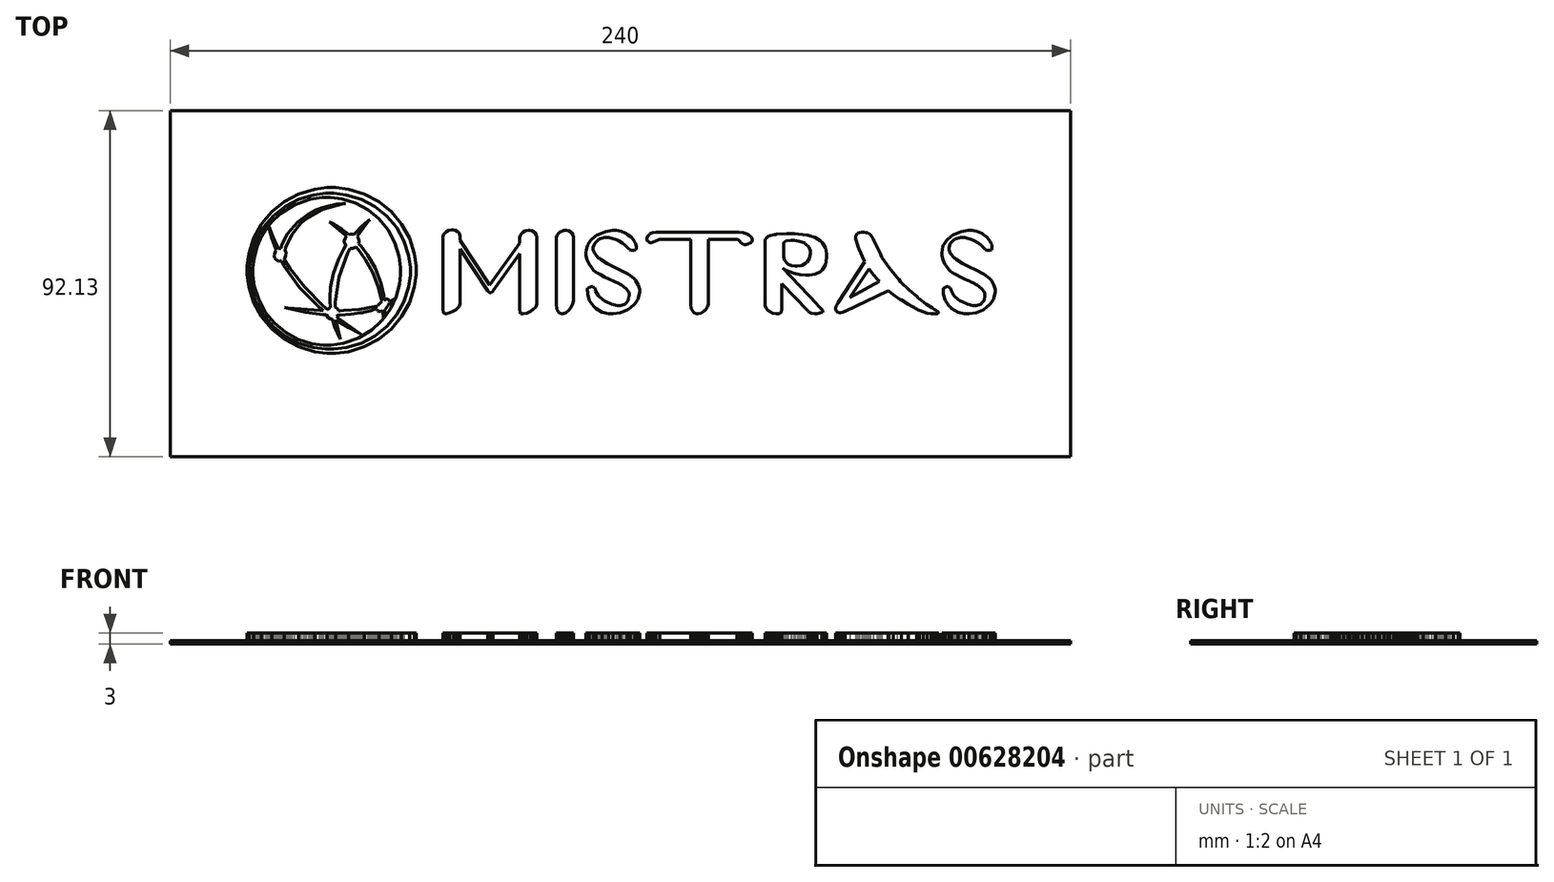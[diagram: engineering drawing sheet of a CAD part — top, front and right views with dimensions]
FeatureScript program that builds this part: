
annotation { "Feature Type Name" : "Feature", "Feature Type Description" : "" }
export const myFeature = defineFeature(function(context is Context, id is Id, definition is map)
    precondition{}
    {
        {
            var Q0;
            Q0=qCreatedBy(makeId("Top.planeOp"),FACE);
            var sketch = newSketch(context, id + "F0", { "sketchPlane" : qUnion([Q0])});
            skLineSegment(sketch, "E0.bottom", {"start": v(-94.91, 44.04) * mm, "end": v(105.09, 44.04) * mm, "construction": true});
            skLineSegment(sketch, "E0.top", {"start": v(-94.91, -8.1) * mm, "end": v(105.09, -8.1) * mm, "construction": true});
            skLineSegment(sketch, "E0.left", {"start": v(-94.91, 44.04) * mm, "end": v(-94.91, -8.1) * mm, "construction": true});
            skLineSegment(sketch, "E0.right", {"start": v(105.09, 44.04) * mm, "end": v(105.09, -8.1) * mm, "construction": true});
            skLineSegment(sketch, "E1", {"start": v(-21.8, 26) * mm, "end": v(-28.84, 16.06) * mm});
            skLineSegment(sketch, "E2", {"start": v(-28.84, 16.06) * mm, "end": v(-28.9, 15.99) * mm});
            skLineSegment(sketch, "E3", {"start": v(-28.9, 15.99) * mm, "end": v(-29.42, 15.62) * mm});
            skLineSegment(sketch, "E4", {"start": v(-29.42, 15.62) * mm, "end": v(-29.6, 15.62) * mm});
            skLineSegment(sketch, "E5", {"start": v(-29.6, 15.62) * mm, "end": v(-29.76, 15.62) * mm});
            skLineSegment(sketch, "E6", {"start": v(-29.76, 15.62) * mm, "end": v(-30.22, 15.97) * mm});
            skLineSegment(sketch, "E7", {"start": v(-30.22, 15.97) * mm, "end": v(-30.26, 16.05) * mm});
            skLineSegment(sketch, "E8", {"start": v(-30.26, 16.05) * mm, "end": v(-37.6, 27.26) * mm});
            skLineSegment(sketch, "E9", {"start": v(-37.6, 27.26) * mm, "end": v(-37.6, 12.97) * mm});
            skLineSegment(sketch, "E10", {"start": v(-37.6, 12.97) * mm, "end": v(-37.6, 12.7) * mm});
            skLineSegment(sketch, "E11", {"start": v(-37.6, 12.7) * mm, "end": v(-37.96, 11.88) * mm});
            skLineSegment(sketch, "E12", {"start": v(-37.96, 11.88) * mm, "end": v(-38.8, 11.04) * mm});
            skLineSegment(sketch, "E13", {"start": v(-38.8, 11.04) * mm, "end": v(-39.05, 10.88) * mm});
            skLineSegment(sketch, "E14", {"start": v(-39.05, 10.88) * mm, "end": v(-39.3, 10.73) * mm});
            skLineSegment(sketch, "E15", {"start": v(-39.3, 10.73) * mm, "end": v(-40.42, 10.17) * mm});
            skLineSegment(sketch, "E16", {"start": v(-40.42, 10.17) * mm, "end": v(-41.31, 9.94) * mm});
            skLineSegment(sketch, "E17", {"start": v(-41.31, 9.94) * mm, "end": v(-41.61, 9.94) * mm});
            skLineSegment(sketch, "E18", {"start": v(-41.61, 9.94) * mm, "end": v(-41.74, 9.94) * mm});
            skLineSegment(sketch, "E19", {"start": v(-41.74, 9.94) * mm, "end": v(-42.13, 10.22) * mm});
            skLineSegment(sketch, "E20", {"start": v(-42.13, 10.22) * mm, "end": v(-42.14, 10.27) * mm});
            skLineSegment(sketch, "E21", {"start": v(-42.14, 10.27) * mm, "end": v(-42.15, 10.33) * mm});
            skLineSegment(sketch, "E22", {"start": v(-42.15, 10.33) * mm, "end": v(-42.2, 11.12) * mm});
            skLineSegment(sketch, "E23", {"start": v(-42.2, 11.12) * mm, "end": v(-42.2, 11.22) * mm});
            skLineSegment(sketch, "E24", {"start": v(-42.2, 11.22) * mm, "end": v(-42.21, 11.32) * mm});
            skLineSegment(sketch, "E25", {"start": v(-42.21, 11.32) * mm, "end": v(-42.23, 12.56) * mm});
            skLineSegment(sketch, "E26", {"start": v(-42.23, 12.56) * mm, "end": v(-42.23, 12.97) * mm});
            skLineSegment(sketch, "E27", {"start": v(-42.23, 12.97) * mm, "end": v(-42.23, 30.16) * mm});
            skLineSegment(sketch, "E28", {"start": v(-42.23, 30.16) * mm, "end": v(-42.23, 30.38) * mm});
            skLineSegment(sketch, "E29", {"start": v(-42.23, 30.38) * mm, "end": v(-42.05, 31.03) * mm});
            skLineSegment(sketch, "E30", {"start": v(-42.05, 31.03) * mm, "end": v(-41.6, 31.63) * mm});
            skLineSegment(sketch, "E31", {"start": v(-41.6, 31.63) * mm, "end": v(-41.48, 31.73) * mm});
            skLineSegment(sketch, "E32", {"start": v(-41.48, 31.73) * mm, "end": v(-41.35, 31.83) * mm});
            skLineSegment(sketch, "E33", {"start": v(-41.35, 31.83) * mm, "end": v(-40.67, 32.2) * mm});
            skLineSegment(sketch, "E34", {"start": v(-40.67, 32.2) * mm, "end": v(-39.98, 32.35) * mm});
            skLineSegment(sketch, "E35", {"start": v(-39.98, 32.35) * mm, "end": v(-39.75, 32.35) * mm});
            skLineSegment(sketch, "E36", {"start": v(-39.75, 32.35) * mm, "end": v(-39.53, 32.35) * mm});
            skLineSegment(sketch, "E37", {"start": v(-39.53, 32.35) * mm, "end": v(-38.87, 32.21) * mm});
            skLineSegment(sketch, "E38", {"start": v(-38.87, 32.21) * mm, "end": v(-38.28, 31.88) * mm});
            skLineSegment(sketch, "E39", {"start": v(-38.28, 31.88) * mm, "end": v(-38.18, 31.78) * mm});
            skLineSegment(sketch, "E40", {"start": v(-38.18, 31.78) * mm, "end": v(-38.09, 31.7) * mm});
            skLineSegment(sketch, "E41", {"start": v(-38.09, 31.7) * mm, "end": v(-37.74, 31.15) * mm});
            skLineSegment(sketch, "E42", {"start": v(-37.74, 31.15) * mm, "end": v(-37.6, 30.57) * mm});
            skLineSegment(sketch, "E43", {"start": v(-37.6, 30.57) * mm, "end": v(-37.6, 30.38) * mm});
            skLineSegment(sketch, "E44", {"start": v(-37.6, 30.38) * mm, "end": v(-37.6, 29.51) * mm});
            skLineSegment(sketch, "E45", {"start": v(-37.6, 29.51) * mm, "end": v(-29.82, 17.54) * mm});
            skLineSegment(sketch, "E46", {"start": v(-29.82, 17.54) * mm, "end": v(-21.8, 28.81) * mm});
            skLineSegment(sketch, "E47", {"start": v(-21.8, 28.81) * mm, "end": v(-21.8, 30) * mm});
            skLineSegment(sketch, "E48", {"start": v(-21.8, 30) * mm, "end": v(-21.8, 30.22) * mm});
            skLineSegment(sketch, "E49", {"start": v(-21.8, 30.22) * mm, "end": v(-21.6, 30.87) * mm});
            skLineSegment(sketch, "E50", {"start": v(-21.6, 30.87) * mm, "end": v(-21.17, 31.47) * mm});
            skLineSegment(sketch, "E51", {"start": v(-21.17, 31.47) * mm, "end": v(-21.04, 31.57) * mm});
            skLineSegment(sketch, "E52", {"start": v(-21.04, 31.57) * mm, "end": v(-20.92, 31.67) * mm});
            skLineSegment(sketch, "E53", {"start": v(-20.92, 31.67) * mm, "end": v(-20.23, 32.03) * mm});
            skLineSegment(sketch, "E54", {"start": v(-20.23, 32.03) * mm, "end": v(-19.54, 32.19) * mm});
            skLineSegment(sketch, "E55", {"start": v(-19.54, 32.19) * mm, "end": v(-19.31, 32.19) * mm});
            skLineSegment(sketch, "E56", {"start": v(-19.31, 32.19) * mm, "end": v(-19.1, 32.19) * mm});
            skLineSegment(sketch, "E57", {"start": v(-19.1, 32.19) * mm, "end": v(-18.44, 32.05) * mm});
            skLineSegment(sketch, "E58", {"start": v(-18.44, 32.05) * mm, "end": v(-17.85, 31.72) * mm});
            skLineSegment(sketch, "E59", {"start": v(-17.85, 31.72) * mm, "end": v(-17.75, 31.62) * mm});
            skLineSegment(sketch, "E60", {"start": v(-17.75, 31.62) * mm, "end": v(-17.65, 31.53) * mm});
            skLineSegment(sketch, "E61", {"start": v(-17.65, 31.53) * mm, "end": v(-17.3, 30.99) * mm});
            skLineSegment(sketch, "E62", {"start": v(-17.3, 30.99) * mm, "end": v(-17.15, 30.41) * mm});
            skLineSegment(sketch, "E63", {"start": v(-17.15, 30.41) * mm, "end": v(-17.15, 30.22) * mm});
            skLineSegment(sketch, "E64", {"start": v(-17.15, 30.22) * mm, "end": v(-17.15, 12.8) * mm});
            skLineSegment(sketch, "E65", {"start": v(-17.15, 12.8) * mm, "end": v(-17.15, 12.54) * mm});
            skLineSegment(sketch, "E66", {"start": v(-17.15, 12.54) * mm, "end": v(-17.51, 11.75) * mm});
            skLineSegment(sketch, "E67", {"start": v(-17.51, 11.75) * mm, "end": v(-18.35, 10.96) * mm});
            skLineSegment(sketch, "E68", {"start": v(-18.35, 10.96) * mm, "end": v(-18.59, 10.81) * mm});
            skLineSegment(sketch, "E69", {"start": v(-18.59, 10.81) * mm, "end": v(-18.83, 10.67) * mm});
            skLineSegment(sketch, "E70", {"start": v(-18.83, 10.67) * mm, "end": v(-19.94, 10.16) * mm});
            skLineSegment(sketch, "E71", {"start": v(-19.94, 10.16) * mm, "end": v(-20.83, 9.94) * mm});
            skLineSegment(sketch, "E72", {"start": v(-20.83, 9.94) * mm, "end": v(-21.12, 9.94) * mm});
            skLineSegment(sketch, "E73", {"start": v(-21.12, 9.94) * mm, "end": v(-21.23, 9.94) * mm});
            skLineSegment(sketch, "E74", {"start": v(-21.23, 9.94) * mm, "end": v(-21.54, 10.02) * mm});
            skLineSegment(sketch, "E75", {"start": v(-21.54, 10.02) * mm, "end": v(-21.7, 10.23) * mm});
            skLineSegment(sketch, "E76", {"start": v(-21.7, 10.23) * mm, "end": v(-21.7, 10.29) * mm});
            skLineSegment(sketch, "E77", {"start": v(-21.7, 10.29) * mm, "end": v(-21.71, 10.35) * mm});
            skLineSegment(sketch, "E78", {"start": v(-21.71, 10.35) * mm, "end": v(-21.77, 11.08) * mm});
            skLineSegment(sketch, "E79", {"start": v(-21.77, 11.08) * mm, "end": v(-21.77, 11.17) * mm});
            skLineSegment(sketch, "E80", {"start": v(-21.77, 11.17) * mm, "end": v(-21.77, 11.26) * mm});
            skLineSegment(sketch, "E81", {"start": v(-21.77, 11.26) * mm, "end": v(-21.8, 12.42) * mm});
            skLineSegment(sketch, "E82", {"start": v(-21.8, 12.42) * mm, "end": v(-21.8, 12.8) * mm});
            skLineSegment(sketch, "E83", {"start": v(-21.8, 12.8) * mm, "end": v(-21.8, 26) * mm});
            skLineSegment(sketch, "E84", {"start": v(-7.37, 30.21) * mm, "end": v(-7.37, 13.75) * mm});
            skLineSegment(sketch, "E85", {"start": v(-7.37, 13.75) * mm, "end": v(-7.37, 13.45) * mm});
            skLineSegment(sketch, "E86", {"start": v(-7.37, 13.45) * mm, "end": v(-7.63, 12.54) * mm});
            skLineSegment(sketch, "E87", {"start": v(-7.63, 12.54) * mm, "end": v(-8.22, 11.48) * mm});
            skLineSegment(sketch, "E88", {"start": v(-8.22, 11.48) * mm, "end": v(-8.39, 11.26) * mm});
            skLineSegment(sketch, "E89", {"start": v(-8.39, 11.26) * mm, "end": v(-8.56, 11.04) * mm});
            skLineSegment(sketch, "E90", {"start": v(-8.56, 11.04) * mm, "end": v(-9.4, 10.27) * mm});
            skLineSegment(sketch, "E91", {"start": v(-9.4, 10.27) * mm, "end": v(-10.17, 9.94) * mm});
            skLineSegment(sketch, "E92", {"start": v(-10.17, 9.94) * mm, "end": v(-10.42, 9.94) * mm});
            skLineSegment(sketch, "E93", {"start": v(-10.42, 9.94) * mm, "end": v(-10.65, 9.94) * mm});
            skLineSegment(sketch, "E94", {"start": v(-10.65, 9.94) * mm, "end": v(-11.23, 10.26) * mm});
            skLineSegment(sketch, "E95", {"start": v(-11.23, 10.26) * mm, "end": v(-11.3, 10.33) * mm});
            skLineSegment(sketch, "E96", {"start": v(-11.3, 10.33) * mm, "end": v(-11.38, 10.4) * mm});
            skLineSegment(sketch, "E97", {"start": v(-11.38, 10.4) * mm, "end": v(-11.86, 11.19) * mm});
            skLineSegment(sketch, "E98", {"start": v(-11.86, 11.19) * mm, "end": v(-11.88, 11.28) * mm});
            skLineSegment(sketch, "E99", {"start": v(-11.88, 11.28) * mm, "end": v(-11.9, 11.37) * mm});
            skLineSegment(sketch, "E100", {"start": v(-11.9, 11.37) * mm, "end": v(-12.02, 12.44) * mm});
            skLineSegment(sketch, "E101", {"start": v(-12.02, 12.44) * mm, "end": v(-12.02, 12.8) * mm});
            skLineSegment(sketch, "E102", {"start": v(-12.02, 12.8) * mm, "end": v(-12.02, 30) * mm});
            skLineSegment(sketch, "E103", {"start": v(-12.02, 30) * mm, "end": v(-12.02, 30.21) * mm});
            skLineSegment(sketch, "E104", {"start": v(-12.02, 30.21) * mm, "end": v(-11.83, 30.86) * mm});
            skLineSegment(sketch, "E105", {"start": v(-11.83, 30.86) * mm, "end": v(-11.4, 31.46) * mm});
            skLineSegment(sketch, "E106", {"start": v(-11.4, 31.46) * mm, "end": v(-11.26, 31.56) * mm});
            skLineSegment(sketch, "E107", {"start": v(-11.26, 31.56) * mm, "end": v(-11.14, 31.67) * mm});
            skLineSegment(sketch, "E108", {"start": v(-11.14, 31.67) * mm, "end": v(-9.94, 32.18) * mm});
            skLineSegment(sketch, "E109", {"start": v(-9.94, 32.18) * mm, "end": v(-9.53, 32.18) * mm});
            skLineSegment(sketch, "E110", {"start": v(-9.53, 32.18) * mm, "end": v(-9.32, 32.18) * mm});
            skLineSegment(sketch, "E111", {"start": v(-9.32, 32.18) * mm, "end": v(-8.66, 32.04) * mm});
            skLineSegment(sketch, "E112", {"start": v(-8.66, 32.04) * mm, "end": v(-8.07, 31.71) * mm});
            skLineSegment(sketch, "E113", {"start": v(-8.07, 31.71) * mm, "end": v(-7.97, 31.62) * mm});
            skLineSegment(sketch, "E114", {"start": v(-7.97, 31.62) * mm, "end": v(-7.87, 31.52) * mm});
            skLineSegment(sketch, "E115", {"start": v(-7.87, 31.52) * mm, "end": v(-7.52, 30.98) * mm});
            skLineSegment(sketch, "E116", {"start": v(-7.52, 30.98) * mm, "end": v(-7.37, 30.4) * mm});
            skLineSegment(sketch, "E117", {"start": v(-7.37, 30.4) * mm, "end": v(-7.37, 30.21) * mm});
            skLineSegment(sketch, "E118", {"start": v(-1.61, 16.35) * mm, "end": v(-1.55, 16.07) * mm});
            skLineSegment(sketch, "E119", {"start": v(-1.55, 16.07) * mm, "end": v(-0.81, 14.79) * mm});
            skLineSegment(sketch, "E120", {"start": v(-0.81, 14.79) * mm, "end": v(0.46, 13.65) * mm});
            skLineSegment(sketch, "E121", {"start": v(0.46, 13.65) * mm, "end": v(0.8, 13.44) * mm});
            skLineSegment(sketch, "E122", {"start": v(0.8, 13.44) * mm, "end": v(1.12, 13.23) * mm});
            skLineSegment(sketch, "E123", {"start": v(1.12, 13.23) * mm, "end": v(2.78, 12.5) * mm});
            skLineSegment(sketch, "E124", {"start": v(2.78, 12.5) * mm, "end": v(4.25, 12.2) * mm});
            skLineSegment(sketch, "E125", {"start": v(4.25, 12.2) * mm, "end": v(4.74, 12.2) * mm});
            skLineSegment(sketch, "E126", {"start": v(4.74, 12.2) * mm, "end": v(5.16, 12.2) * mm});
            skLineSegment(sketch, "E127", {"start": v(5.16, 12.2) * mm, "end": v(6.33, 12.57) * mm});
            skLineSegment(sketch, "E128", {"start": v(6.33, 12.57) * mm, "end": v(6.44, 12.65) * mm});
            skLineSegment(sketch, "E129", {"start": v(6.44, 12.65) * mm, "end": v(6.55, 12.72) * mm});
            skLineSegment(sketch, "E130", {"start": v(6.55, 12.72) * mm, "end": v(7.2, 13.6) * mm});
            skLineSegment(sketch, "E131", {"start": v(7.2, 13.6) * mm, "end": v(7.22, 13.7) * mm});
            skLineSegment(sketch, "E132", {"start": v(7.22, 13.7) * mm, "end": v(7.24, 13.8) * mm});
            skLineSegment(sketch, "E133", {"start": v(7.24, 13.8) * mm, "end": v(7.37, 14.53) * mm});
            skLineSegment(sketch, "E134", {"start": v(7.37, 14.53) * mm, "end": v(7.37, 14.57) * mm});
            skLineSegment(sketch, "E135", {"start": v(7.37, 14.57) * mm, "end": v(7.38, 14.62) * mm});
            skLineSegment(sketch, "E136", {"start": v(7.38, 14.62) * mm, "end": v(7.41, 15.06) * mm});
            skLineSegment(sketch, "E137", {"start": v(7.41, 15.06) * mm, "end": v(7.41, 15.2) * mm});
            skLineSegment(sketch, "E138", {"start": v(7.41, 15.2) * mm, "end": v(7.41, 15.4) * mm});
            skLineSegment(sketch, "E139", {"start": v(7.41, 15.4) * mm, "end": v(7.19, 15.98) * mm});
            skLineSegment(sketch, "E140", {"start": v(7.19, 15.98) * mm, "end": v(6.52, 16.77) * mm});
            skLineSegment(sketch, "E141", {"start": v(6.52, 16.77) * mm, "end": v(5.4, 17.58) * mm});
            skLineSegment(sketch, "E142", {"start": v(5.4, 17.58) * mm, "end": v(4.23, 18.22) * mm});
            skLineSegment(sketch, "E143", {"start": v(4.23, 18.22) * mm, "end": v(3.83, 18.4) * mm});
            skLineSegment(sketch, "E144", {"start": v(3.83, 18.4) * mm, "end": v(3.42, 18.6) * mm});
            skLineSegment(sketch, "E145", {"start": v(3.42, 18.6) * mm, "end": v(2.2, 19.17) * mm});
            skLineSegment(sketch, "E146", {"start": v(2.2, 19.17) * mm, "end": v(0.86, 19.82) * mm});
            skLineSegment(sketch, "E147", {"start": v(0.86, 19.82) * mm, "end": v(-0.18, 20.33) * mm});
            skLineSegment(sketch, "E148", {"start": v(-0.18, 20.33) * mm, "end": v(-0.73, 20.62) * mm});
            skLineSegment(sketch, "E149", {"start": v(-0.73, 20.62) * mm, "end": v(-0.9, 20.72) * mm});
            skLineSegment(sketch, "E150", {"start": v(-0.9, 20.72) * mm, "end": v(-1.1, 20.84) * mm});
            skLineSegment(sketch, "E151", {"start": v(-1.1, 20.84) * mm, "end": v(-2.03, 21.6) * mm});
            skLineSegment(sketch, "E152", {"start": v(-2.03, 21.6) * mm, "end": v(-2.9, 22.64) * mm});
            skLineSegment(sketch, "E153", {"start": v(-2.9, 22.64) * mm, "end": v(-3.07, 22.9) * mm});
            skLineSegment(sketch, "E154", {"start": v(-3.07, 22.9) * mm, "end": v(-3.24, 23.14) * mm});
            skLineSegment(sketch, "E155", {"start": v(-3.24, 23.14) * mm, "end": v(-3.83, 24.44) * mm});
            skLineSegment(sketch, "E156", {"start": v(-3.83, 24.44) * mm, "end": v(-4.07, 25.66) * mm});
            skLineSegment(sketch, "E157", {"start": v(-4.07, 25.66) * mm, "end": v(-4.07, 26.06) * mm});
            skLineSegment(sketch, "E158", {"start": v(-4.07, 26.06) * mm, "end": v(-4.07, 26.3) * mm});
            skLineSegment(sketch, "E159", {"start": v(-4.07, 26.3) * mm, "end": v(-3.97, 26.98) * mm});
            skLineSegment(sketch, "E160", {"start": v(-3.97, 26.98) * mm, "end": v(-3.73, 28) * mm});
            skLineSegment(sketch, "E161", {"start": v(-3.73, 28) * mm, "end": v(-3.66, 28.22) * mm});
            skLineSegment(sketch, "E162", {"start": v(-3.66, 28.22) * mm, "end": v(-3.59, 28.46) * mm});
            skLineSegment(sketch, "E163", {"start": v(-3.59, 28.46) * mm, "end": v(-2.83, 29.6) * mm});
            skLineSegment(sketch, "E164", {"start": v(-2.83, 29.6) * mm, "end": v(-1.52, 30.7) * mm});
            skLineSegment(sketch, "E165", {"start": v(-1.52, 30.7) * mm, "end": v(-1.18, 30.9) * mm});
            skLineSegment(sketch, "E166", {"start": v(-1.18, 30.9) * mm, "end": v(-0.84, 31.12) * mm});
            skLineSegment(sketch, "E167", {"start": v(-0.84, 31.12) * mm, "end": v(1.04, 31.86) * mm});
            skLineSegment(sketch, "E168", {"start": v(1.04, 31.86) * mm, "end": v(2.96, 32.18) * mm});
            skLineSegment(sketch, "E169", {"start": v(2.96, 32.18) * mm, "end": v(3.6, 32.18) * mm});
            skLineSegment(sketch, "E170", {"start": v(3.6, 32.18) * mm, "end": v(4, 32.18) * mm});
            skLineSegment(sketch, "E171", {"start": v(4, 32.18) * mm, "end": v(5.22, 31.96) * mm});
            skLineSegment(sketch, "E172", {"start": v(5.22, 31.96) * mm, "end": v(6.47, 31.42) * mm});
            skLineSegment(sketch, "E173", {"start": v(6.47, 31.42) * mm, "end": v(6.71, 31.27) * mm});
            skLineSegment(sketch, "E174", {"start": v(6.71, 31.27) * mm, "end": v(6.95, 31.12) * mm});
            skLineSegment(sketch, "E175", {"start": v(6.95, 31.12) * mm, "end": v(7.91, 30.37) * mm});
            skLineSegment(sketch, "E176", {"start": v(7.91, 30.37) * mm, "end": v(8.57, 29.64) * mm});
            skLineSegment(sketch, "E177", {"start": v(8.57, 29.64) * mm, "end": v(8.66, 29.5) * mm});
            skLineSegment(sketch, "E178", {"start": v(8.66, 29.5) * mm, "end": v(8.74, 29.35) * mm});
            skLineSegment(sketch, "E179", {"start": v(8.74, 29.35) * mm, "end": v(9.06, 28.76) * mm});
            skLineSegment(sketch, "E180", {"start": v(9.06, 28.76) * mm, "end": v(9.24, 28.35) * mm});
            skLineSegment(sketch, "E181", {"start": v(9.24, 28.35) * mm, "end": v(9.25, 28.3) * mm});
            skLineSegment(sketch, "E182", {"start": v(9.25, 28.3) * mm, "end": v(9.27, 28.24) * mm});
            skLineSegment(sketch, "E183", {"start": v(9.27, 28.24) * mm, "end": v(9.33, 27.85) * mm});
            skLineSegment(sketch, "E184", {"start": v(9.33, 27.85) * mm, "end": v(9.33, 27.73) * mm});
            skLineSegment(sketch, "E185", {"start": v(9.33, 27.73) * mm, "end": v(9.33, 27.62) * mm});
            skLineSegment(sketch, "E186", {"start": v(9.33, 27.62) * mm, "end": v(9.29, 27.33) * mm});
            skLineSegment(sketch, "E187", {"start": v(9.29, 27.33) * mm, "end": v(9.28, 27.3) * mm});
            skLineSegment(sketch, "E188", {"start": v(9.28, 27.3) * mm, "end": v(9.27, 27.28) * mm});
            skLineSegment(sketch, "E189", {"start": v(9.27, 27.28) * mm, "end": v(9.18, 27.06) * mm});
            skLineSegment(sketch, "E190", {"start": v(9.18, 27.06) * mm, "end": v(9.17, 27.04) * mm});
            skLineSegment(sketch, "E191", {"start": v(9.17, 27.04) * mm, "end": v(9.1, 27.03) * mm});
            skLineSegment(sketch, "E192", {"start": v(9.1, 27.03) * mm, "end": v(8.6, 26.93) * mm});
            skLineSegment(sketch, "E193", {"start": v(8.6, 26.93) * mm, "end": v(8.56, 26.92) * mm});
            skLineSegment(sketch, "E194", {"start": v(8.56, 26.92) * mm, "end": v(8.53, 26.91) * mm});
            skLineSegment(sketch, "E195", {"start": v(8.53, 26.91) * mm, "end": v(8.28, 26.88) * mm});
            skLineSegment(sketch, "E196", {"start": v(8.28, 26.88) * mm, "end": v(8.2, 26.88) * mm});
            skLineSegment(sketch, "E197", {"start": v(8.2, 26.88) * mm, "end": v(8.05, 26.88) * mm});
            skLineSegment(sketch, "E198", {"start": v(8.05, 26.88) * mm, "end": v(7.62, 27.02) * mm});
            skLineSegment(sketch, "E199", {"start": v(7.62, 27.02) * mm, "end": v(7.57, 27.05) * mm});
            skLineSegment(sketch, "E200", {"start": v(7.57, 27.05) * mm, "end": v(7.53, 27.08) * mm});
            skLineSegment(sketch, "E201", {"start": v(7.53, 27.08) * mm, "end": v(7.2, 27.38) * mm});
            skLineSegment(sketch, "E202", {"start": v(7.2, 27.38) * mm, "end": v(6.72, 27.9) * mm});
            skLineSegment(sketch, "E203", {"start": v(6.72, 27.9) * mm, "end": v(6.6, 28.03) * mm});
            skLineSegment(sketch, "E204", {"start": v(6.6, 28.03) * mm, "end": v(6.49, 28.16) * mm});
            skLineSegment(sketch, "E205", {"start": v(6.49, 28.16) * mm, "end": v(5.7, 28.8) * mm});
            skLineSegment(sketch, "E206", {"start": v(5.7, 28.8) * mm, "end": v(4.62, 29.42) * mm});
            skLineSegment(sketch, "E207", {"start": v(4.62, 29.42) * mm, "end": v(4.36, 29.54) * mm});
            skLineSegment(sketch, "E208", {"start": v(4.36, 29.54) * mm, "end": v(4.1, 29.66) * mm});
            skLineSegment(sketch, "E209", {"start": v(4.1, 29.66) * mm, "end": v(2.03, 30.25) * mm});
            skLineSegment(sketch, "E210", {"start": v(2.03, 30.25) * mm, "end": v(1.33, 30.25) * mm});
            skLineSegment(sketch, "E211", {"start": v(1.33, 30.25) * mm, "end": v(0.86, 30.25) * mm});
            skLineSegment(sketch, "E212", {"start": v(0.86, 30.25) * mm, "end": v(-0.41, 29.91) * mm});
            skLineSegment(sketch, "E213", {"start": v(-0.41, 29.91) * mm, "end": v(-0.55, 29.84) * mm});
            skLineSegment(sketch, "E214", {"start": v(-0.55, 29.84) * mm, "end": v(-0.68, 29.77) * mm});
            skLineSegment(sketch, "E215", {"start": v(-0.68, 29.77) * mm, "end": v(-1.7, 28.82) * mm});
            skLineSegment(sketch, "E216", {"start": v(-1.7, 28.82) * mm, "end": v(-1.78, 28.7) * mm});
            skLineSegment(sketch, "E217", {"start": v(-1.78, 28.7) * mm, "end": v(-1.84, 28.57) * mm});
            skLineSegment(sketch, "E218", {"start": v(-1.84, 28.57) * mm, "end": v(-2.18, 27.7) * mm});
            skLineSegment(sketch, "E219", {"start": v(-2.18, 27.7) * mm, "end": v(-2.18, 27.4) * mm});
            skLineSegment(sketch, "E220", {"start": v(-2.18, 27.4) * mm, "end": v(-2.18, 27.05) * mm});
            skLineSegment(sketch, "E221", {"start": v(-2.18, 27.05) * mm, "end": v(-1.76, 25.98) * mm});
            skLineSegment(sketch, "E222", {"start": v(-1.76, 25.98) * mm, "end": v(-0.77, 24.88) * mm});
            skLineSegment(sketch, "E223", {"start": v(-0.77, 24.88) * mm, "end": v(-0.5, 24.67) * mm});
            skLineSegment(sketch, "E224", {"start": v(-0.5, 24.67) * mm, "end": v(-0.21, 24.46) * mm});
            skLineSegment(sketch, "E225", {"start": v(-0.21, 24.46) * mm, "end": v(1.58, 23.36) * mm});
            skLineSegment(sketch, "E226", {"start": v(1.58, 23.36) * mm, "end": v(3.87, 22.2) * mm});
            skLineSegment(sketch, "E227", {"start": v(3.87, 22.2) * mm, "end": v(4.4, 21.96) * mm});
            skLineSegment(sketch, "E228", {"start": v(4.4, 21.96) * mm, "end": v(4.94, 21.72) * mm});
            skLineSegment(sketch, "E229", {"start": v(4.94, 21.72) * mm, "end": v(7.13, 20.52) * mm});
            skLineSegment(sketch, "E230", {"start": v(7.13, 20.52) * mm, "end": v(8.68, 19.32) * mm});
            skLineSegment(sketch, "E231", {"start": v(8.68, 19.32) * mm, "end": v(8.9, 19.08) * mm});
            skLineSegment(sketch, "E232", {"start": v(8.9, 19.08) * mm, "end": v(9.1, 18.85) * mm});
            skLineSegment(sketch, "E233", {"start": v(9.1, 18.85) * mm, "end": v(9.86, 17.6) * mm});
            skLineSegment(sketch, "E234", {"start": v(9.86, 17.6) * mm, "end": v(10.18, 16.42) * mm});
            skLineSegment(sketch, "E235", {"start": v(10.18, 16.42) * mm, "end": v(10.18, 16.02) * mm});
            skLineSegment(sketch, "E236", {"start": v(10.18, 16.02) * mm, "end": v(10.18, 15.83) * mm});
            skLineSegment(sketch, "E237", {"start": v(10.18, 15.83) * mm, "end": v(10.08, 15.25) * mm});
            skLineSegment(sketch, "E238", {"start": v(10.08, 15.25) * mm, "end": v(9.85, 14.27) * mm});
            skLineSegment(sketch, "E239", {"start": v(9.85, 14.27) * mm, "end": v(9.79, 14.03) * mm});
            skLineSegment(sketch, "E240", {"start": v(9.79, 14.03) * mm, "end": v(9.72, 13.79) * mm});
            skLineSegment(sketch, "E241", {"start": v(9.72, 13.79) * mm, "end": v(8.97, 12.62) * mm});
            skLineSegment(sketch, "E242", {"start": v(8.97, 12.62) * mm, "end": v(7.65, 11.48) * mm});
            skLineSegment(sketch, "E243", {"start": v(7.65, 11.48) * mm, "end": v(7.3, 11.26) * mm});
            skLineSegment(sketch, "E244", {"start": v(7.3, 11.26) * mm, "end": v(6.95, 11.04) * mm});
            skLineSegment(sketch, "E245", {"start": v(6.95, 11.04) * mm, "end": v(5.06, 10.26) * mm});
            skLineSegment(sketch, "E246", {"start": v(5.06, 10.26) * mm, "end": v(3.15, 9.92) * mm});
            skLineSegment(sketch, "E247", {"start": v(3.15, 9.92) * mm, "end": v(2.52, 9.92) * mm});
            skLineSegment(sketch, "E248", {"start": v(2.52, 9.92) * mm, "end": v(1.94, 9.92) * mm});
            skLineSegment(sketch, "E249", {"start": v(1.94, 9.92) * mm, "end": v(0.22, 10.37) * mm});
            skLineSegment(sketch, "E250", {"start": v(0.22, 10.37) * mm, "end": v(-1.48, 11.41) * mm});
            skLineSegment(sketch, "E251", {"start": v(-1.48, 11.41) * mm, "end": v(-1.79, 11.7) * mm});
            skLineSegment(sketch, "E252", {"start": v(-1.79, 11.7) * mm, "end": v(-2.1, 12) * mm});
            skLineSegment(sketch, "E253", {"start": v(-2.1, 12) * mm, "end": v(-3.18, 13.6) * mm});
            skLineSegment(sketch, "E254", {"start": v(-3.18, 13.6) * mm, "end": v(-3.64, 15.17) * mm});
            skLineSegment(sketch, "E255", {"start": v(-3.64, 15.17) * mm, "end": v(-3.64, 15.69) * mm});
            skLineSegment(sketch, "E256", {"start": v(-3.64, 15.69) * mm, "end": v(-3.65, 15.76) * mm});
            skLineSegment(sketch, "E257", {"start": v(-3.65, 15.76) * mm, "end": v(-3.7, 16.2) * mm});
            skLineSegment(sketch, "E258", {"start": v(-3.7, 16.2) * mm, "end": v(-3.7, 16.35) * mm});
            skLineSegment(sketch, "E259", {"start": v(-3.7, 16.35) * mm, "end": v(-3.7, 16.46) * mm});
            skLineSegment(sketch, "E260", {"start": v(-3.7, 16.46) * mm, "end": v(-3.6, 16.78) * mm});
            skLineSegment(sketch, "E261", {"start": v(-3.6, 16.78) * mm, "end": v(-3.57, 16.8) * mm});
            skLineSegment(sketch, "E262", {"start": v(-3.57, 16.8) * mm, "end": v(-3.55, 16.84) * mm});
            skLineSegment(sketch, "E263", {"start": v(-3.55, 16.84) * mm, "end": v(-3.15, 17.06) * mm});
            skLineSegment(sketch, "E264", {"start": v(-3.15, 17.06) * mm, "end": v(-3.08, 17.07) * mm});
            skLineSegment(sketch, "E265", {"start": v(-3.08, 17.07) * mm, "end": v(-3.02, 17.09) * mm});
            skLineSegment(sketch, "E266", {"start": v(-3.02, 17.09) * mm, "end": v(-2.66, 17.17) * mm});
            skLineSegment(sketch, "E267", {"start": v(-2.66, 17.17) * mm, "end": v(-2.53, 17.17) * mm});
            skLineSegment(sketch, "E268", {"start": v(-2.53, 17.17) * mm, "end": v(-2.38, 17.17) * mm});
            skLineSegment(sketch, "E269", {"start": v(-2.38, 17.17) * mm, "end": v(-1.96, 16.98) * mm});
            skLineSegment(sketch, "E270", {"start": v(-1.96, 16.98) * mm, "end": v(-1.92, 16.94) * mm});
            skLineSegment(sketch, "E271", {"start": v(-1.92, 16.94) * mm, "end": v(-1.9, 16.9) * mm});
            skLineSegment(sketch, "E272", {"start": v(-1.9, 16.9) * mm, "end": v(-1.63, 16.4) * mm});
            skLineSegment(sketch, "E273", {"start": v(-1.63, 16.4) * mm, "end": v(-1.61, 16.35) * mm});
            skLineSegment(sketch, "E274", {"start": v(16, 29.78) * mm, "end": v(15.6, 29.78) * mm});
            skLineSegment(sketch, "E275", {"start": v(15.6, 29.78) * mm, "end": v(14.56, 29.43) * mm});
            skLineSegment(sketch, "E276", {"start": v(14.56, 29.43) * mm, "end": v(14.4, 29.35) * mm});
            skLineSegment(sketch, "E277", {"start": v(14.4, 29.35) * mm, "end": v(14.26, 29.28) * mm});
            skLineSegment(sketch, "E278", {"start": v(14.26, 29.28) * mm, "end": v(13.66, 29.03) * mm});
            skLineSegment(sketch, "E279", {"start": v(13.66, 29.03) * mm, "end": v(13.33, 28.92) * mm});
            skLineSegment(sketch, "E280", {"start": v(13.33, 28.92) * mm, "end": v(13.22, 28.92) * mm});
            skLineSegment(sketch, "E281", {"start": v(13.22, 28.92) * mm, "end": v(13.04, 28.92) * mm});
            skLineSegment(sketch, "E282", {"start": v(13.04, 28.92) * mm, "end": v(12.56, 29.13) * mm});
            skLineSegment(sketch, "E283", {"start": v(12.56, 29.13) * mm, "end": v(12.5, 29.18) * mm});
            skLineSegment(sketch, "E284", {"start": v(12.5, 29.18) * mm, "end": v(12.44, 29.22) * mm});
            skLineSegment(sketch, "E285", {"start": v(12.44, 29.22) * mm, "end": v(12.14, 29.75) * mm});
            skLineSegment(sketch, "E286", {"start": v(12.14, 29.75) * mm, "end": v(12.14, 29.92) * mm});
            skLineSegment(sketch, "E287", {"start": v(12.14, 29.92) * mm, "end": v(12.14, 30.09) * mm});
            skLineSegment(sketch, "E288", {"start": v(12.14, 30.09) * mm, "end": v(12.31, 30.59) * mm});
            skLineSegment(sketch, "E289", {"start": v(12.31, 30.59) * mm, "end": v(12.72, 31.09) * mm});
            skLineSegment(sketch, "E290", {"start": v(12.72, 31.09) * mm, "end": v(12.84, 31.18) * mm});
            skLineSegment(sketch, "E291", {"start": v(12.84, 31.18) * mm, "end": v(12.96, 31.27) * mm});
            skLineSegment(sketch, "E292", {"start": v(12.96, 31.27) * mm, "end": v(13.68, 31.6) * mm});
            skLineSegment(sketch, "E293", {"start": v(13.68, 31.6) * mm, "end": v(14.53, 31.74) * mm});
            skLineSegment(sketch, "E294", {"start": v(14.53, 31.74) * mm, "end": v(14.81, 31.74) * mm});
            skLineSegment(sketch, "E295", {"start": v(14.81, 31.74) * mm, "end": v(36.2, 31.74) * mm});
            skLineSegment(sketch, "E296", {"start": v(36.2, 31.74) * mm, "end": v(36.6, 31.74) * mm});
            skLineSegment(sketch, "E297", {"start": v(36.6, 31.74) * mm, "end": v(37.77, 31.57) * mm});
            skLineSegment(sketch, "E298", {"start": v(37.77, 31.57) * mm, "end": v(38.88, 31.2) * mm});
            skLineSegment(sketch, "E299", {"start": v(38.88, 31.2) * mm, "end": v(39.08, 31.09) * mm});
            skLineSegment(sketch, "E300", {"start": v(39.08, 31.09) * mm, "end": v(39.27, 30.98) * mm});
            skLineSegment(sketch, "E301", {"start": v(39.27, 30.98) * mm, "end": v(39.96, 30.4) * mm});
            skLineSegment(sketch, "E302", {"start": v(39.96, 30.4) * mm, "end": v(40.25, 29.86) * mm});
            skLineSegment(sketch, "E303", {"start": v(40.25, 29.86) * mm, "end": v(40.25, 29.68) * mm});
            skLineSegment(sketch, "E304", {"start": v(40.25, 29.68) * mm, "end": v(40.25, 29.53) * mm});
            skLineSegment(sketch, "E305", {"start": v(40.25, 29.53) * mm, "end": v(40.05, 29.07) * mm});
            skLineSegment(sketch, "E306", {"start": v(40.05, 29.07) * mm, "end": v(39.58, 28.74) * mm});
            skLineSegment(sketch, "E307", {"start": v(39.58, 28.74) * mm, "end": v(39.44, 28.7) * mm});
            skLineSegment(sketch, "E308", {"start": v(39.44, 28.7) * mm, "end": v(39.3, 28.65) * mm});
            skLineSegment(sketch, "E309", {"start": v(39.3, 28.65) * mm, "end": v(38.54, 28.43) * mm});
            skLineSegment(sketch, "E310", {"start": v(38.54, 28.43) * mm, "end": v(38.28, 28.43) * mm});
            skLineSegment(sketch, "E311", {"start": v(38.28, 28.43) * mm, "end": v(37.95, 28.43) * mm});
            skLineSegment(sketch, "E312", {"start": v(37.95, 28.43) * mm, "end": v(37.08, 29) * mm});
            skLineSegment(sketch, "E313", {"start": v(37.08, 29) * mm, "end": v(36.98, 29.1) * mm});
            skLineSegment(sketch, "E314", {"start": v(36.98, 29.1) * mm, "end": v(36.88, 29.22) * mm});
            skLineSegment(sketch, "E315", {"start": v(36.88, 29.22) * mm, "end": v(36.46, 29.62) * mm});
            skLineSegment(sketch, "E316", {"start": v(36.46, 29.62) * mm, "end": v(36.18, 29.78) * mm});
            skLineSegment(sketch, "E317", {"start": v(36.18, 29.78) * mm, "end": v(36.1, 29.78) * mm});
            skLineSegment(sketch, "E318", {"start": v(36.1, 29.78) * mm, "end": v(28.48, 29.78) * mm});
            skLineSegment(sketch, "E319", {"start": v(28.48, 29.78) * mm, "end": v(28.48, 12.8) * mm});
            skLineSegment(sketch, "E320", {"start": v(28.48, 12.8) * mm, "end": v(28.48, 12.55) * mm});
            skLineSegment(sketch, "E321", {"start": v(28.48, 12.55) * mm, "end": v(28.25, 11.8) * mm});
            skLineSegment(sketch, "E322", {"start": v(28.25, 11.8) * mm, "end": v(27.72, 11) * mm});
            skLineSegment(sketch, "E323", {"start": v(27.72, 11) * mm, "end": v(27.57, 10.86) * mm});
            skLineSegment(sketch, "E324", {"start": v(27.57, 10.86) * mm, "end": v(27.41, 10.7) * mm});
            skLineSegment(sketch, "E325", {"start": v(27.41, 10.7) * mm, "end": v(26.63, 10.17) * mm});
            skLineSegment(sketch, "E326", {"start": v(26.63, 10.17) * mm, "end": v(25.9, 9.94) * mm});
            skLineSegment(sketch, "E327", {"start": v(25.9, 9.94) * mm, "end": v(25.65, 9.94) * mm});
            skLineSegment(sketch, "E328", {"start": v(25.65, 9.94) * mm, "end": v(25.4, 9.94) * mm});
            skLineSegment(sketch, "E329", {"start": v(25.4, 9.94) * mm, "end": v(24.73, 10.23) * mm});
            skLineSegment(sketch, "E330", {"start": v(24.73, 10.23) * mm, "end": v(24.65, 10.29) * mm});
            skLineSegment(sketch, "E331", {"start": v(24.65, 10.29) * mm, "end": v(24.57, 10.35) * mm});
            skLineSegment(sketch, "E332", {"start": v(24.57, 10.35) * mm, "end": v(24.03, 11.16) * mm});
            skLineSegment(sketch, "E333", {"start": v(24.03, 11.16) * mm, "end": v(24, 11.26) * mm});
            skLineSegment(sketch, "E334", {"start": v(24, 11.26) * mm, "end": v(23.97, 11.37) * mm});
            skLineSegment(sketch, "E335", {"start": v(23.97, 11.37) * mm, "end": v(23.84, 12.44) * mm});
            skLineSegment(sketch, "E336", {"start": v(23.84, 12.44) * mm, "end": v(23.84, 12.8) * mm});
            skLineSegment(sketch, "E337", {"start": v(23.84, 12.8) * mm, "end": v(23.84, 29.78) * mm});
            skLineSegment(sketch, "E338", {"start": v(23.84, 29.78) * mm, "end": v(16, 29.78) * mm});
            skLineSegment(sketch, "E339", {"start": v(48.12, 11.53) * mm, "end": v(48.12, 11.24) * mm});
            skLineSegment(sketch, "E340", {"start": v(48.12, 11.24) * mm, "end": v(48, 10.43) * mm});
            skLineSegment(sketch, "E341", {"start": v(48, 10.43) * mm, "end": v(47.97, 10.37) * mm});
            skLineSegment(sketch, "E342", {"start": v(47.97, 10.37) * mm, "end": v(47.95, 10.32) * mm});
            skLineSegment(sketch, "E343", {"start": v(47.95, 10.32) * mm, "end": v(47.47, 10) * mm});
            skLineSegment(sketch, "E344", {"start": v(47.47, 10) * mm, "end": v(47.4, 10) * mm});
            skLineSegment(sketch, "E345", {"start": v(47.4, 10) * mm, "end": v(47.33, 9.98) * mm});
            skLineSegment(sketch, "E346", {"start": v(47.33, 9.98) * mm, "end": v(46.93, 9.94) * mm});
            skLineSegment(sketch, "E347", {"start": v(46.93, 9.94) * mm, "end": v(46.8, 9.94) * mm});
            skLineSegment(sketch, "E348", {"start": v(46.8, 9.94) * mm, "end": v(46.5, 9.94) * mm});
            skLineSegment(sketch, "E349", {"start": v(46.5, 9.94) * mm, "end": v(45.65, 10.14) * mm});
            skLineSegment(sketch, "E350", {"start": v(45.65, 10.14) * mm, "end": v(44.76, 10.6) * mm});
            skLineSegment(sketch, "E351", {"start": v(44.76, 10.6) * mm, "end": v(44.59, 10.74) * mm});
            skLineSegment(sketch, "E352", {"start": v(44.59, 10.74) * mm, "end": v(44.42, 10.87) * mm});
            skLineSegment(sketch, "E353", {"start": v(44.42, 10.87) * mm, "end": v(43.83, 11.54) * mm});
            skLineSegment(sketch, "E354", {"start": v(43.83, 11.54) * mm, "end": v(43.57, 12.16) * mm});
            skLineSegment(sketch, "E355", {"start": v(43.57, 12.16) * mm, "end": v(43.57, 12.37) * mm});
            skLineSegment(sketch, "E356", {"start": v(43.57, 12.37) * mm, "end": v(43.57, 29.3) * mm});
            skLineSegment(sketch, "E357", {"start": v(43.57, 29.3) * mm, "end": v(43.57, 29.44) * mm});
            skLineSegment(sketch, "E358", {"start": v(43.57, 29.44) * mm, "end": v(43.69, 29.82) * mm});
            skLineSegment(sketch, "E359", {"start": v(43.69, 29.82) * mm, "end": v(43.71, 29.85) * mm});
            skLineSegment(sketch, "E360", {"start": v(43.71, 29.85) * mm, "end": v(43.73, 29.88) * mm});
            skLineSegment(sketch, "E361", {"start": v(43.73, 29.88) * mm, "end": v(44.23, 30.37) * mm});
            skLineSegment(sketch, "E362", {"start": v(44.23, 30.37) * mm, "end": v(44.3, 30.44) * mm});
            skLineSegment(sketch, "E363", {"start": v(44.3, 30.44) * mm, "end": v(44.38, 30.5) * mm});
            skLineSegment(sketch, "E364", {"start": v(44.38, 30.5) * mm, "end": v(45.06, 30.8) * mm});
            skLineSegment(sketch, "E365", {"start": v(45.06, 30.8) * mm, "end": v(46.15, 31.05) * mm});
            skLineSegment(sketch, "E366", {"start": v(46.15, 31.05) * mm, "end": v(46.43, 31.09) * mm});
            skLineSegment(sketch, "E367", {"start": v(46.43, 31.09) * mm, "end": v(46.7, 31.13) * mm});
            skLineSegment(sketch, "E368", {"start": v(46.7, 31.13) * mm, "end": v(49.4, 31.33) * mm});
            skLineSegment(sketch, "E369", {"start": v(49.4, 31.33) * mm, "end": v(50.3, 31.33) * mm});
            skLineSegment(sketch, "E370", {"start": v(50.3, 31.33) * mm, "end": v(51.48, 31.33) * mm});
            skLineSegment(sketch, "E371", {"start": v(51.48, 31.33) * mm, "end": v(54.61, 30.98) * mm});
            skLineSegment(sketch, "E372", {"start": v(54.61, 30.98) * mm, "end": v(54.98, 30.9) * mm});
            skLineSegment(sketch, "E373", {"start": v(54.98, 30.9) * mm, "end": v(55.35, 30.84) * mm});
            skLineSegment(sketch, "E374", {"start": v(55.35, 30.84) * mm, "end": v(57, 30.26) * mm});
            skLineSegment(sketch, "E375", {"start": v(57, 30.26) * mm, "end": v(58.4, 29.36) * mm});
            skLineSegment(sketch, "E376", {"start": v(58.4, 29.36) * mm, "end": v(58.64, 29.14) * mm});
            skLineSegment(sketch, "E377", {"start": v(58.64, 29.14) * mm, "end": v(58.87, 28.91) * mm});
            skLineSegment(sketch, "E378", {"start": v(58.87, 28.91) * mm, "end": v(59.71, 27.56) * mm});
            skLineSegment(sketch, "E379", {"start": v(59.71, 27.56) * mm, "end": v(60.07, 26.04) * mm});
            skLineSegment(sketch, "E380", {"start": v(60.07, 26.04) * mm, "end": v(60.07, 25.54) * mm});
            skLineSegment(sketch, "E381", {"start": v(60.07, 25.54) * mm, "end": v(60.07, 24.92) * mm});
            skLineSegment(sketch, "E382", {"start": v(60.07, 24.92) * mm, "end": v(59.71, 23.06) * mm});
            skLineSegment(sketch, "E383", {"start": v(59.71, 23.06) * mm, "end": v(58.87, 21.63) * mm});
            skLineSegment(sketch, "E384", {"start": v(58.87, 21.63) * mm, "end": v(58.64, 21.42) * mm});
            skLineSegment(sketch, "E385", {"start": v(58.64, 21.42) * mm, "end": v(58.4, 21.22) * mm});
            skLineSegment(sketch, "E386", {"start": v(58.4, 21.22) * mm, "end": v(56.99, 20.5) * mm});
            skLineSegment(sketch, "E387", {"start": v(56.99, 20.5) * mm, "end": v(55.42, 20.2) * mm});
            skLineSegment(sketch, "E388", {"start": v(55.42, 20.2) * mm, "end": v(54.9, 20.2) * mm});
            skLineSegment(sketch, "E389", {"start": v(54.9, 20.2) * mm, "end": v(54.41, 20.2) * mm});
            skLineSegment(sketch, "E390", {"start": v(54.41, 20.2) * mm, "end": v(52.95, 20.39) * mm});
            skLineSegment(sketch, "E391", {"start": v(52.95, 20.39) * mm, "end": v(51.26, 20.8) * mm});
            skLineSegment(sketch, "E392", {"start": v(51.26, 20.8) * mm, "end": v(50.92, 20.92) * mm});
            skLineSegment(sketch, "E393", {"start": v(50.92, 20.92) * mm, "end": v(50.57, 21.04) * mm});
            skLineSegment(sketch, "E394", {"start": v(50.57, 21.04) * mm, "end": v(49.23, 21.6) * mm});
            skLineSegment(sketch, "E395", {"start": v(49.23, 21.6) * mm, "end": v(48.4, 22.08) * mm});
            skLineSegment(sketch, "E396", {"start": v(48.4, 22.08) * mm, "end": v(48.3, 22.16) * mm});
            skLineSegment(sketch, "E397", {"start": v(48.3, 22.16) * mm, "end": v(57.41, 12.53) * mm});
            skLineSegment(sketch, "E398", {"start": v(57.41, 12.53) * mm, "end": v(57.65, 12.28) * mm});
            skLineSegment(sketch, "E399", {"start": v(57.65, 12.28) * mm, "end": v(58.53, 11.34) * mm});
            skLineSegment(sketch, "E400", {"start": v(58.53, 11.34) * mm, "end": v(59, 10.8) * mm});
            skLineSegment(sketch, "E401", {"start": v(59, 10.8) * mm, "end": v(59.02, 10.76) * mm});
            skLineSegment(sketch, "E402", {"start": v(59.02, 10.76) * mm, "end": v(59.05, 10.71) * mm});
            skLineSegment(sketch, "E403", {"start": v(59.05, 10.71) * mm, "end": v(59.02, 10.4) * mm});
            skLineSegment(sketch, "E404", {"start": v(59.02, 10.4) * mm, "end": v(58.98, 10.4) * mm});
            skLineSegment(sketch, "E405", {"start": v(58.98, 10.4) * mm, "end": v(58.83, 10.32) * mm});
            skLineSegment(sketch, "E406", {"start": v(58.83, 10.32) * mm, "end": v(57.5, 9.94) * mm});
            skLineSegment(sketch, "E407", {"start": v(57.5, 9.94) * mm, "end": v(57.07, 9.94) * mm});
            skLineSegment(sketch, "E408", {"start": v(57.07, 9.94) * mm, "end": v(56.8, 9.94) * mm});
            skLineSegment(sketch, "E409", {"start": v(56.8, 9.94) * mm, "end": v(56.07, 10.08) * mm});
            skLineSegment(sketch, "E410", {"start": v(56.07, 10.08) * mm, "end": v(55.98, 10.11) * mm});
            skLineSegment(sketch, "E411", {"start": v(55.98, 10.11) * mm, "end": v(55.9, 10.14) * mm});
            skLineSegment(sketch, "E412", {"start": v(55.9, 10.14) * mm, "end": v(55.1, 10.67) * mm});
            skLineSegment(sketch, "E413", {"start": v(55.1, 10.67) * mm, "end": v(55.02, 10.75) * mm});
            skLineSegment(sketch, "E414", {"start": v(55.02, 10.75) * mm, "end": v(48.12, 17.95) * mm});
            skLineSegment(sketch, "E415", {"start": v(48.12, 17.95) * mm, "end": v(48.12, 11.53) * mm});
            skLineSegment(sketch, "E416", {"start": v(55.69, 26.38) * mm, "end": v(55.69, 26.72) * mm});
            skLineSegment(sketch, "E417", {"start": v(55.69, 26.72) * mm, "end": v(55.33, 27.72) * mm});
            skLineSegment(sketch, "E418", {"start": v(55.33, 27.72) * mm, "end": v(54.47, 28.58) * mm});
            skLineSegment(sketch, "E419", {"start": v(54.47, 28.58) * mm, "end": v(54.23, 28.72) * mm});
            skLineSegment(sketch, "E420", {"start": v(54.23, 28.72) * mm, "end": v(53.99, 28.86) * mm});
            skLineSegment(sketch, "E421", {"start": v(53.99, 28.86) * mm, "end": v(52.66, 29.34) * mm});
            skLineSegment(sketch, "E422", {"start": v(52.66, 29.34) * mm, "end": v(51.32, 29.55) * mm});
            skLineSegment(sketch, "E423", {"start": v(51.32, 29.55) * mm, "end": v(50.88, 29.55) * mm});
            skLineSegment(sketch, "E424", {"start": v(50.88, 29.55) * mm, "end": v(50.46, 29.55) * mm});
            skLineSegment(sketch, "E425", {"start": v(50.46, 29.55) * mm, "end": v(49.32, 29.39) * mm});
            skLineSegment(sketch, "E426", {"start": v(49.32, 29.39) * mm, "end": v(49.22, 29.36) * mm});
            skLineSegment(sketch, "E427", {"start": v(49.22, 29.36) * mm, "end": v(49.1, 29.33) * mm});
            skLineSegment(sketch, "E428", {"start": v(49.1, 29.33) * mm, "end": v(48.74, 29.08) * mm});
            skLineSegment(sketch, "E429", {"start": v(48.74, 29.08) * mm, "end": v(48.58, 28.74) * mm});
            skLineSegment(sketch, "E430", {"start": v(48.58, 28.74) * mm, "end": v(48.58, 28.63) * mm});
            skLineSegment(sketch, "E431", {"start": v(48.58, 28.63) * mm, "end": v(48.58, 25.35) * mm});
            skLineSegment(sketch, "E432", {"start": v(48.58, 25.35) * mm, "end": v(48.58, 25.07) * mm});
            skLineSegment(sketch, "E433", {"start": v(48.58, 25.07) * mm, "end": v(48.83, 24.23) * mm});
            skLineSegment(sketch, "E434", {"start": v(48.83, 24.23) * mm, "end": v(49.41, 23.49) * mm});
            skLineSegment(sketch, "E435", {"start": v(49.41, 23.49) * mm, "end": v(49.58, 23.36) * mm});
            skLineSegment(sketch, "E436", {"start": v(49.58, 23.36) * mm, "end": v(49.75, 23.24) * mm});
            skLineSegment(sketch, "E437", {"start": v(49.75, 23.24) * mm, "end": v(50.67, 22.8) * mm});
            skLineSegment(sketch, "E438", {"start": v(50.67, 22.8) * mm, "end": v(51.64, 22.62) * mm});
            skLineSegment(sketch, "E439", {"start": v(51.64, 22.62) * mm, "end": v(51.96, 22.62) * mm});
            skLineSegment(sketch, "E440", {"start": v(51.96, 22.62) * mm, "end": v(52.31, 22.62) * mm});
            skLineSegment(sketch, "E441", {"start": v(52.31, 22.62) * mm, "end": v(53.37, 22.86) * mm});
            skLineSegment(sketch, "E442", {"start": v(53.37, 22.86) * mm, "end": v(54.4, 23.42) * mm});
            skLineSegment(sketch, "E443", {"start": v(54.4, 23.42) * mm, "end": v(54.58, 23.58) * mm});
            skLineSegment(sketch, "E444", {"start": v(54.58, 23.58) * mm, "end": v(54.77, 23.74) * mm});
            skLineSegment(sketch, "E445", {"start": v(54.77, 23.74) * mm, "end": v(55.41, 24.76) * mm});
            skLineSegment(sketch, "E446", {"start": v(55.41, 24.76) * mm, "end": v(55.69, 25.98) * mm});
            skLineSegment(sketch, "E447", {"start": v(55.69, 25.98) * mm, "end": v(55.69, 26.38) * mm});
            skLineSegment(sketch, "E448", {"start": v(70.7, 31.6) * mm, "end": v(70.88, 31.57) * mm});
            skLineSegment(sketch, "E449", {"start": v(70.88, 31.57) * mm, "end": v(71.7, 31.03) * mm});
            skLineSegment(sketch, "E450", {"start": v(71.7, 31.03) * mm, "end": v(72.48, 29.9) * mm});
            skLineSegment(sketch, "E451", {"start": v(72.48, 29.9) * mm, "end": v(72.62, 29.6) * mm});
            skLineSegment(sketch, "E452", {"start": v(72.62, 29.6) * mm, "end": v(72.76, 29.29) * mm});
            skLineSegment(sketch, "E453", {"start": v(72.76, 29.29) * mm, "end": v(74.32, 25.93) * mm});
            skLineSegment(sketch, "E454", {"start": v(74.32, 25.93) * mm, "end": v(74.48, 25.57) * mm});
            skLineSegment(sketch, "E455", {"start": v(74.48, 25.57) * mm, "end": v(74.8, 25) * mm});
            skLineSegment(sketch, "E456", {"start": v(74.8, 25) * mm, "end": v(76.6, 22.24) * mm});
            skLineSegment(sketch, "E457", {"start": v(76.6, 22.24) * mm, "end": v(78.77, 19.58) * mm});
            skLineSegment(sketch, "E458", {"start": v(78.77, 19.58) * mm, "end": v(79.26, 19.06) * mm});
            skLineSegment(sketch, "E459", {"start": v(79.26, 19.06) * mm, "end": v(79.74, 18.55) * mm});
            skLineSegment(sketch, "E460", {"start": v(79.74, 18.55) * mm, "end": v(82.02, 16.3) * mm});
            skLineSegment(sketch, "E461", {"start": v(82.02, 16.3) * mm, "end": v(84.08, 14.5) * mm});
            skLineSegment(sketch, "E462", {"start": v(84.08, 14.5) * mm, "end": v(84.46, 14.2) * mm});
            skLineSegment(sketch, "E463", {"start": v(84.46, 14.2) * mm, "end": v(84.84, 13.9) * mm});
            skLineSegment(sketch, "E464", {"start": v(84.84, 13.9) * mm, "end": v(86.62, 12.58) * mm});
            skLineSegment(sketch, "E465", {"start": v(86.62, 12.58) * mm, "end": v(88.25, 11.47) * mm});
            skLineSegment(sketch, "E466", {"start": v(88.25, 11.47) * mm, "end": v(88.56, 11.28) * mm});
            skLineSegment(sketch, "E467", {"start": v(88.56, 11.28) * mm, "end": v(88.74, 11.16) * mm});
            skLineSegment(sketch, "E468", {"start": v(88.74, 11.16) * mm, "end": v(89.28, 10.82) * mm});
            skLineSegment(sketch, "E469", {"start": v(89.28, 10.82) * mm, "end": v(89.68, 10.54) * mm});
            skLineSegment(sketch, "E470", {"start": v(89.68, 10.54) * mm, "end": v(89.86, 10.39) * mm});
            skLineSegment(sketch, "E471", {"start": v(89.86, 10.39) * mm, "end": v(89.9, 10.3) * mm});
            skLineSegment(sketch, "E472", {"start": v(89.9, 10.3) * mm, "end": v(89.9, 10.27) * mm});
            skLineSegment(sketch, "E473", {"start": v(89.9, 10.27) * mm, "end": v(89.9, 10.22) * mm});
            skLineSegment(sketch, "E474", {"start": v(89.9, 10.22) * mm, "end": v(89.67, 10.08) * mm});
            skLineSegment(sketch, "E475", {"start": v(89.67, 10.08) * mm, "end": v(89.62, 10.06) * mm});
            skLineSegment(sketch, "E476", {"start": v(89.62, 10.06) * mm, "end": v(89.57, 10.04) * mm});
            skLineSegment(sketch, "E477", {"start": v(89.57, 10.04) * mm, "end": v(88.9, 9.92) * mm});
            skLineSegment(sketch, "E478", {"start": v(88.9, 9.92) * mm, "end": v(88.68, 9.92) * mm});
            skLineSegment(sketch, "E479", {"start": v(88.68, 9.92) * mm, "end": v(88.46, 9.92) * mm});
            skLineSegment(sketch, "E480", {"start": v(88.46, 9.92) * mm, "end": v(87.78, 9.96) * mm});
            skLineSegment(sketch, "E481", {"start": v(87.78, 9.96) * mm, "end": v(86.84, 10.1) * mm});
            skLineSegment(sketch, "E482", {"start": v(86.84, 10.1) * mm, "end": v(85.76, 10.45) * mm});
            skLineSegment(sketch, "E483", {"start": v(85.76, 10.45) * mm, "end": v(84.77, 10.87) * mm});
            skLineSegment(sketch, "E484", {"start": v(84.77, 10.87) * mm, "end": v(84.45, 11.03) * mm});
            skLineSegment(sketch, "E485", {"start": v(84.45, 11.03) * mm, "end": v(83.96, 11.28) * mm});
            skLineSegment(sketch, "E486", {"start": v(83.96, 11.28) * mm, "end": v(81.77, 12.48) * mm});
            skLineSegment(sketch, "E487", {"start": v(81.77, 12.48) * mm, "end": v(79.9, 13.63) * mm});
            skLineSegment(sketch, "E488", {"start": v(79.9, 13.63) * mm, "end": v(79.57, 13.85) * mm});
            skLineSegment(sketch, "E489", {"start": v(79.57, 13.85) * mm, "end": v(79.24, 14.07) * mm});
            skLineSegment(sketch, "E490", {"start": v(79.24, 14.07) * mm, "end": v(77.8, 15.07) * mm});
            skLineSegment(sketch, "E491", {"start": v(77.8, 15.07) * mm, "end": v(76.6, 15.9) * mm});
            skLineSegment(sketch, "E492", {"start": v(76.6, 15.9) * mm, "end": v(76.4, 16.05) * mm});
            skLineSegment(sketch, "E493", {"start": v(76.4, 16.05) * mm, "end": v(64.97, 10.65) * mm});
            skLineSegment(sketch, "E494", {"start": v(64.97, 10.65) * mm, "end": v(64.9, 10.61) * mm});
            skLineSegment(sketch, "E495", {"start": v(64.9, 10.61) * mm, "end": v(64.27, 10.34) * mm});
            skLineSegment(sketch, "E496", {"start": v(64.27, 10.34) * mm, "end": v(64.21, 10.32) * mm});
            skLineSegment(sketch, "E497", {"start": v(64.21, 10.32) * mm, "end": v(64.16, 10.3) * mm});
            skLineSegment(sketch, "E498", {"start": v(64.16, 10.3) * mm, "end": v(63.73, 10.21) * mm});
            skLineSegment(sketch, "E499", {"start": v(63.73, 10.21) * mm, "end": v(63.6, 10.21) * mm});
            skLineSegment(sketch, "E500", {"start": v(63.6, 10.21) * mm, "end": v(63.39, 10.21) * mm});
            skLineSegment(sketch, "E501", {"start": v(63.39, 10.21) * mm, "end": v(62.85, 10.47) * mm});
            skLineSegment(sketch, "E502", {"start": v(62.85, 10.47) * mm, "end": v(62.8, 10.52) * mm});
            skLineSegment(sketch, "E503", {"start": v(62.8, 10.52) * mm, "end": v(62.73, 10.58) * mm});
            skLineSegment(sketch, "E504", {"start": v(62.73, 10.58) * mm, "end": v(62.46, 11.14) * mm});
            skLineSegment(sketch, "E505", {"start": v(62.46, 11.14) * mm, "end": v(62.46, 11.32) * mm});
            skLineSegment(sketch, "E506", {"start": v(62.46, 11.32) * mm, "end": v(62.46, 11.52) * mm});
            skLineSegment(sketch, "E507", {"start": v(62.46, 11.52) * mm, "end": v(62.6, 12.03) * mm});
            skLineSegment(sketch, "E508", {"start": v(62.6, 12.03) * mm, "end": v(62.62, 12.1) * mm});
            skLineSegment(sketch, "E509", {"start": v(62.62, 12.1) * mm, "end": v(62.65, 12.16) * mm});
            skLineSegment(sketch, "E510", {"start": v(62.65, 12.16) * mm, "end": v(63.03, 12.87) * mm});
            skLineSegment(sketch, "E511", {"start": v(63.03, 12.87) * mm, "end": v(63.08, 12.95) * mm});
            skLineSegment(sketch, "E512", {"start": v(63.08, 12.95) * mm, "end": v(70.19, 23.78) * mm});
            skLineSegment(sketch, "E513", {"start": v(70.19, 23.78) * mm, "end": v(70.05, 24.1) * mm});
            skLineSegment(sketch, "E514", {"start": v(70.05, 24.1) * mm, "end": v(68.7, 27.22) * mm});
            skLineSegment(sketch, "E515", {"start": v(68.7, 27.22) * mm, "end": v(68.58, 27.53) * mm});
            skLineSegment(sketch, "E516", {"start": v(68.58, 27.53) * mm, "end": v(68.45, 27.84) * mm});
            skLineSegment(sketch, "E517", {"start": v(68.45, 27.84) * mm, "end": v(68, 29.13) * mm});
            skLineSegment(sketch, "E518", {"start": v(68, 29.13) * mm, "end": v(67.81, 29.97) * mm});
            skLineSegment(sketch, "E519", {"start": v(67.81, 29.97) * mm, "end": v(67.81, 30.25) * mm});
            skLineSegment(sketch, "E520", {"start": v(67.81, 30.25) * mm, "end": v(67.81, 30.52) * mm});
            skLineSegment(sketch, "E521", {"start": v(67.81, 30.52) * mm, "end": v(68.17, 31.27) * mm});
            skLineSegment(sketch, "E522", {"start": v(68.17, 31.27) * mm, "end": v(68.24, 31.33) * mm});
            skLineSegment(sketch, "E523", {"start": v(68.24, 31.33) * mm, "end": v(68.31, 31.39) * mm});
            skLineSegment(sketch, "E524", {"start": v(68.31, 31.39) * mm, "end": v(68.82, 31.6) * mm});
            skLineSegment(sketch, "E525", {"start": v(68.82, 31.6) * mm, "end": v(69.46, 31.68) * mm});
            skLineSegment(sketch, "E526", {"start": v(69.46, 31.68) * mm, "end": v(69.67, 31.68) * mm});
            skLineSegment(sketch, "E527", {"start": v(69.67, 31.68) * mm, "end": v(69.93, 31.68) * mm});
            skLineSegment(sketch, "E528", {"start": v(69.93, 31.68) * mm, "end": v(70.6, 31.6) * mm});
            skLineSegment(sketch, "E529", {"start": v(70.6, 31.6) * mm, "end": v(70.7, 31.6) * mm});
            skLineSegment(sketch, "E530", {"start": v(71.26, 21.97) * mm, "end": v(66.2, 14.3) * mm});
            skLineSegment(sketch, "E531", {"start": v(66.2, 14.3) * mm, "end": v(74.1, 18.63) * mm});
            skLineSegment(sketch, "E532", {"start": v(74.1, 18.63) * mm, "end": v(74.04, 18.7) * mm});
            skLineSegment(sketch, "E533", {"start": v(74.04, 18.7) * mm, "end": v(73.49, 19.24) * mm});
            skLineSegment(sketch, "E534", {"start": v(73.49, 19.24) * mm, "end": v(73.44, 19.29) * mm});
            skLineSegment(sketch, "E535", {"start": v(73.44, 19.29) * mm, "end": v(73.4, 19.34) * mm});
            skLineSegment(sketch, "E536", {"start": v(73.4, 19.34) * mm, "end": v(72.7, 20.13) * mm});
            skLineSegment(sketch, "E537", {"start": v(72.7, 20.13) * mm, "end": v(72.6, 20.25) * mm});
            skLineSegment(sketch, "E538", {"start": v(72.6, 20.25) * mm, "end": v(72.5, 20.36) * mm});
            skLineSegment(sketch, "E539", {"start": v(72.5, 20.36) * mm, "end": v(71.39, 21.8) * mm});
            skLineSegment(sketch, "E540", {"start": v(71.39, 21.8) * mm, "end": v(71.26, 21.97) * mm});
            skLineSegment(sketch, "E541", {"start": v(93.17, 16.35) * mm, "end": v(93.24, 16.07) * mm});
            skLineSegment(sketch, "E542", {"start": v(93.24, 16.07) * mm, "end": v(93.98, 14.79) * mm});
            skLineSegment(sketch, "E543", {"start": v(93.98, 14.79) * mm, "end": v(95.24, 13.65) * mm});
            skLineSegment(sketch, "E544", {"start": v(95.24, 13.65) * mm, "end": v(95.58, 13.44) * mm});
            skLineSegment(sketch, "E545", {"start": v(95.58, 13.44) * mm, "end": v(95.91, 13.23) * mm});
            skLineSegment(sketch, "E546", {"start": v(95.91, 13.23) * mm, "end": v(97.56, 12.5) * mm});
            skLineSegment(sketch, "E547", {"start": v(97.56, 12.5) * mm, "end": v(99.04, 12.2) * mm});
            skLineSegment(sketch, "E548", {"start": v(99.04, 12.2) * mm, "end": v(99.53, 12.2) * mm});
            skLineSegment(sketch, "E549", {"start": v(99.53, 12.2) * mm, "end": v(99.95, 12.2) * mm});
            skLineSegment(sketch, "E550", {"start": v(99.95, 12.2) * mm, "end": v(101.12, 12.57) * mm});
            skLineSegment(sketch, "E551", {"start": v(101.12, 12.57) * mm, "end": v(101.23, 12.65) * mm});
            skLineSegment(sketch, "E552", {"start": v(101.23, 12.65) * mm, "end": v(101.34, 12.72) * mm});
            skLineSegment(sketch, "E553", {"start": v(101.34, 12.72) * mm, "end": v(102, 13.6) * mm});
            skLineSegment(sketch, "E554", {"start": v(102, 13.6) * mm, "end": v(102.01, 13.69) * mm});
            skLineSegment(sketch, "E555", {"start": v(102.01, 13.69) * mm, "end": v(102.03, 13.79) * mm});
            skLineSegment(sketch, "E556", {"start": v(102.03, 13.79) * mm, "end": v(102.15, 14.52) * mm});
            skLineSegment(sketch, "E557", {"start": v(102.15, 14.52) * mm, "end": v(102.16, 14.57) * mm});
            skLineSegment(sketch, "E558", {"start": v(102.16, 14.57) * mm, "end": v(102.16, 14.62) * mm});
            skLineSegment(sketch, "E559", {"start": v(102.16, 14.62) * mm, "end": v(102.2, 15.06) * mm});
            skLineSegment(sketch, "E560", {"start": v(102.2, 15.06) * mm, "end": v(102.2, 15.2) * mm});
            skLineSegment(sketch, "E561", {"start": v(102.2, 15.2) * mm, "end": v(102.2, 15.4) * mm});
            skLineSegment(sketch, "E562", {"start": v(102.2, 15.4) * mm, "end": v(101.97, 15.98) * mm});
            skLineSegment(sketch, "E563", {"start": v(101.97, 15.98) * mm, "end": v(101.3, 16.77) * mm});
            skLineSegment(sketch, "E564", {"start": v(101.3, 16.77) * mm, "end": v(100.18, 17.58) * mm});
            skLineSegment(sketch, "E565", {"start": v(100.18, 17.58) * mm, "end": v(99.02, 18.21) * mm});
            skLineSegment(sketch, "E566", {"start": v(99.02, 18.21) * mm, "end": v(98.62, 18.4) * mm});
            skLineSegment(sketch, "E567", {"start": v(98.62, 18.4) * mm, "end": v(98.21, 18.6) * mm});
            skLineSegment(sketch, "E568", {"start": v(98.21, 18.6) * mm, "end": v(96.98, 19.17) * mm});
            skLineSegment(sketch, "E569", {"start": v(96.98, 19.17) * mm, "end": v(95.64, 19.81) * mm});
            skLineSegment(sketch, "E570", {"start": v(95.64, 19.81) * mm, "end": v(94.6, 20.33) * mm});
            skLineSegment(sketch, "E571", {"start": v(94.6, 20.33) * mm, "end": v(94.05, 20.62) * mm});
            skLineSegment(sketch, "E572", {"start": v(94.05, 20.62) * mm, "end": v(93.88, 20.72) * mm});
            skLineSegment(sketch, "E573", {"start": v(93.88, 20.72) * mm, "end": v(93.68, 20.84) * mm});
            skLineSegment(sketch, "E574", {"start": v(93.68, 20.84) * mm, "end": v(92.75, 21.6) * mm});
            skLineSegment(sketch, "E575", {"start": v(92.75, 21.6) * mm, "end": v(91.88, 22.64) * mm});
            skLineSegment(sketch, "E576", {"start": v(91.88, 22.64) * mm, "end": v(91.71, 22.9) * mm});
            skLineSegment(sketch, "E577", {"start": v(91.71, 22.9) * mm, "end": v(91.54, 23.14) * mm});
            skLineSegment(sketch, "E578", {"start": v(91.54, 23.14) * mm, "end": v(90.96, 24.44) * mm});
            skLineSegment(sketch, "E579", {"start": v(90.96, 24.44) * mm, "end": v(90.71, 25.66) * mm});
            skLineSegment(sketch, "E580", {"start": v(90.71, 25.66) * mm, "end": v(90.71, 26.06) * mm});
            skLineSegment(sketch, "E581", {"start": v(90.71, 26.06) * mm, "end": v(90.71, 26.3) * mm});
            skLineSegment(sketch, "E582", {"start": v(90.71, 26.3) * mm, "end": v(90.81, 26.98) * mm});
            skLineSegment(sketch, "E583", {"start": v(90.81, 26.98) * mm, "end": v(91.06, 28) * mm});
            skLineSegment(sketch, "E584", {"start": v(91.06, 28) * mm, "end": v(91.13, 28.22) * mm});
            skLineSegment(sketch, "E585", {"start": v(91.13, 28.22) * mm, "end": v(91.2, 28.46) * mm});
            skLineSegment(sketch, "E586", {"start": v(91.2, 28.46) * mm, "end": v(91.96, 29.6) * mm});
            skLineSegment(sketch, "E587", {"start": v(91.96, 29.6) * mm, "end": v(93.26, 30.7) * mm});
            skLineSegment(sketch, "E588", {"start": v(93.26, 30.7) * mm, "end": v(93.6, 30.9) * mm});
            skLineSegment(sketch, "E589", {"start": v(93.6, 30.9) * mm, "end": v(93.95, 31.12) * mm});
            skLineSegment(sketch, "E590", {"start": v(93.95, 31.12) * mm, "end": v(95.83, 31.86) * mm});
            skLineSegment(sketch, "E591", {"start": v(95.83, 31.86) * mm, "end": v(97.75, 32.18) * mm});
            skLineSegment(sketch, "E592", {"start": v(97.75, 32.18) * mm, "end": v(98.39, 32.18) * mm});
            skLineSegment(sketch, "E593", {"start": v(98.39, 32.18) * mm, "end": v(98.8, 32.18) * mm});
            skLineSegment(sketch, "E594", {"start": v(98.8, 32.18) * mm, "end": v(100, 31.96) * mm});
            skLineSegment(sketch, "E595", {"start": v(100, 31.96) * mm, "end": v(101.26, 31.42) * mm});
            skLineSegment(sketch, "E596", {"start": v(101.26, 31.42) * mm, "end": v(101.5, 31.27) * mm});
            skLineSegment(sketch, "E597", {"start": v(101.5, 31.27) * mm, "end": v(101.74, 31.12) * mm});
            skLineSegment(sketch, "E598", {"start": v(101.74, 31.12) * mm, "end": v(102.7, 30.37) * mm});
            skLineSegment(sketch, "E599", {"start": v(102.7, 30.37) * mm, "end": v(103.36, 29.64) * mm});
            skLineSegment(sketch, "E600", {"start": v(103.36, 29.64) * mm, "end": v(103.44, 29.5) * mm});
            skLineSegment(sketch, "E601", {"start": v(103.44, 29.5) * mm, "end": v(103.53, 29.35) * mm});
            skLineSegment(sketch, "E602", {"start": v(103.53, 29.35) * mm, "end": v(103.85, 28.76) * mm});
            skLineSegment(sketch, "E603", {"start": v(103.85, 28.76) * mm, "end": v(104.03, 28.35) * mm});
            skLineSegment(sketch, "E604", {"start": v(104.03, 28.35) * mm, "end": v(104.04, 28.3) * mm});
            skLineSegment(sketch, "E605", {"start": v(104.04, 28.3) * mm, "end": v(104.05, 28.24) * mm});
            skLineSegment(sketch, "E606", {"start": v(104.05, 28.24) * mm, "end": v(104.12, 27.85) * mm});
            skLineSegment(sketch, "E607", {"start": v(104.12, 27.85) * mm, "end": v(104.12, 27.72) * mm});
            skLineSegment(sketch, "E608", {"start": v(104.12, 27.72) * mm, "end": v(104.12, 27.62) * mm});
            skLineSegment(sketch, "E609", {"start": v(104.12, 27.62) * mm, "end": v(104.07, 27.33) * mm});
            skLineSegment(sketch, "E610", {"start": v(104.07, 27.33) * mm, "end": v(104.07, 27.3) * mm});
            skLineSegment(sketch, "E611", {"start": v(104.07, 27.3) * mm, "end": v(104.05, 27.28) * mm});
            skLineSegment(sketch, "E612", {"start": v(104.05, 27.28) * mm, "end": v(103.97, 27.06) * mm});
            skLineSegment(sketch, "E613", {"start": v(103.97, 27.06) * mm, "end": v(103.96, 27.04) * mm});
            skLineSegment(sketch, "E614", {"start": v(103.96, 27.04) * mm, "end": v(103.9, 27.03) * mm});
            skLineSegment(sketch, "E615", {"start": v(103.9, 27.03) * mm, "end": v(103.39, 26.93) * mm});
            skLineSegment(sketch, "E616", {"start": v(103.39, 26.93) * mm, "end": v(103.35, 26.92) * mm});
            skLineSegment(sketch, "E617", {"start": v(103.35, 26.92) * mm, "end": v(103.32, 26.91) * mm});
            skLineSegment(sketch, "E618", {"start": v(103.32, 26.91) * mm, "end": v(103.07, 26.88) * mm});
            skLineSegment(sketch, "E619", {"start": v(103.07, 26.88) * mm, "end": v(102.99, 26.88) * mm});
            skLineSegment(sketch, "E620", {"start": v(102.99, 26.88) * mm, "end": v(102.83, 26.88) * mm});
            skLineSegment(sketch, "E621", {"start": v(102.83, 26.88) * mm, "end": v(102.4, 27.02) * mm});
            skLineSegment(sketch, "E622", {"start": v(102.4, 27.02) * mm, "end": v(102.36, 27.05) * mm});
            skLineSegment(sketch, "E623", {"start": v(102.36, 27.05) * mm, "end": v(102.32, 27.08) * mm});
            skLineSegment(sketch, "E624", {"start": v(102.32, 27.08) * mm, "end": v(101.99, 27.38) * mm});
            skLineSegment(sketch, "E625", {"start": v(101.99, 27.38) * mm, "end": v(101.5, 27.9) * mm});
            skLineSegment(sketch, "E626", {"start": v(101.5, 27.9) * mm, "end": v(101.4, 28.03) * mm});
            skLineSegment(sketch, "E627", {"start": v(101.4, 28.03) * mm, "end": v(101.27, 28.16) * mm});
            skLineSegment(sketch, "E628", {"start": v(101.27, 28.16) * mm, "end": v(100.48, 28.8) * mm});
            skLineSegment(sketch, "E629", {"start": v(100.48, 28.8) * mm, "end": v(99.4, 29.42) * mm});
            skLineSegment(sketch, "E630", {"start": v(99.4, 29.42) * mm, "end": v(99.15, 29.54) * mm});
            skLineSegment(sketch, "E631", {"start": v(99.15, 29.54) * mm, "end": v(98.9, 29.66) * mm});
            skLineSegment(sketch, "E632", {"start": v(98.9, 29.66) * mm, "end": v(96.8, 30.25) * mm});
            skLineSegment(sketch, "E633", {"start": v(96.8, 30.25) * mm, "end": v(96.12, 30.25) * mm});
            skLineSegment(sketch, "E634", {"start": v(96.12, 30.25) * mm, "end": v(95.65, 30.25) * mm});
            skLineSegment(sketch, "E635", {"start": v(95.65, 30.25) * mm, "end": v(94.38, 29.91) * mm});
            skLineSegment(sketch, "E636", {"start": v(94.38, 29.91) * mm, "end": v(94.24, 29.84) * mm});
            skLineSegment(sketch, "E637", {"start": v(94.24, 29.84) * mm, "end": v(94.1, 29.77) * mm});
            skLineSegment(sketch, "E638", {"start": v(94.1, 29.77) * mm, "end": v(93.08, 28.82) * mm});
            skLineSegment(sketch, "E639", {"start": v(93.08, 28.82) * mm, "end": v(93.01, 28.7) * mm});
            skLineSegment(sketch, "E640", {"start": v(93.01, 28.7) * mm, "end": v(92.95, 28.57) * mm});
            skLineSegment(sketch, "E641", {"start": v(92.95, 28.57) * mm, "end": v(92.6, 27.7) * mm});
            skLineSegment(sketch, "E642", {"start": v(92.6, 27.7) * mm, "end": v(92.6, 27.4) * mm});
            skLineSegment(sketch, "E643", {"start": v(92.6, 27.4) * mm, "end": v(92.6, 27.04) * mm});
            skLineSegment(sketch, "E644", {"start": v(92.6, 27.04) * mm, "end": v(93.03, 25.98) * mm});
            skLineSegment(sketch, "E645", {"start": v(93.03, 25.98) * mm, "end": v(94.01, 24.88) * mm});
            skLineSegment(sketch, "E646", {"start": v(94.01, 24.88) * mm, "end": v(94.3, 24.67) * mm});
            skLineSegment(sketch, "E647", {"start": v(94.3, 24.67) * mm, "end": v(94.58, 24.46) * mm});
            skLineSegment(sketch, "E648", {"start": v(94.58, 24.46) * mm, "end": v(96.36, 23.36) * mm});
            skLineSegment(sketch, "E649", {"start": v(96.36, 23.36) * mm, "end": v(98.66, 22.2) * mm});
            skLineSegment(sketch, "E650", {"start": v(98.66, 22.2) * mm, "end": v(99.2, 21.96) * mm});
            skLineSegment(sketch, "E651", {"start": v(99.2, 21.96) * mm, "end": v(99.73, 21.72) * mm});
            skLineSegment(sketch, "E652", {"start": v(99.73, 21.72) * mm, "end": v(101.91, 20.51) * mm});
            skLineSegment(sketch, "E653", {"start": v(101.91, 20.51) * mm, "end": v(103.47, 19.32) * mm});
            skLineSegment(sketch, "E654", {"start": v(103.47, 19.32) * mm, "end": v(103.68, 19.08) * mm});
            skLineSegment(sketch, "E655", {"start": v(103.68, 19.08) * mm, "end": v(103.9, 18.84) * mm});
            skLineSegment(sketch, "E656", {"start": v(103.9, 18.84) * mm, "end": v(104.64, 17.6) * mm});
            skLineSegment(sketch, "E657", {"start": v(104.64, 17.6) * mm, "end": v(104.96, 16.42) * mm});
            skLineSegment(sketch, "E658", {"start": v(104.96, 16.42) * mm, "end": v(104.96, 16.02) * mm});
            skLineSegment(sketch, "E659", {"start": v(104.96, 16.02) * mm, "end": v(104.96, 15.83) * mm});
            skLineSegment(sketch, "E660", {"start": v(104.96, 15.83) * mm, "end": v(104.86, 15.25) * mm});
            skLineSegment(sketch, "E661", {"start": v(104.86, 15.25) * mm, "end": v(104.64, 14.27) * mm});
            skLineSegment(sketch, "E662", {"start": v(104.64, 14.27) * mm, "end": v(104.57, 14.03) * mm});
            skLineSegment(sketch, "E663", {"start": v(104.57, 14.03) * mm, "end": v(104.5, 13.79) * mm});
            skLineSegment(sketch, "E664", {"start": v(104.5, 13.79) * mm, "end": v(103.75, 12.61) * mm});
            skLineSegment(sketch, "E665", {"start": v(103.75, 12.61) * mm, "end": v(102.43, 11.48) * mm});
            skLineSegment(sketch, "E666", {"start": v(102.43, 11.48) * mm, "end": v(102.09, 11.26) * mm});
            skLineSegment(sketch, "E667", {"start": v(102.09, 11.26) * mm, "end": v(101.74, 11.03) * mm});
            skLineSegment(sketch, "E668", {"start": v(101.74, 11.03) * mm, "end": v(99.84, 10.25) * mm});
            skLineSegment(sketch, "E669", {"start": v(99.84, 10.25) * mm, "end": v(97.94, 9.92) * mm});
            skLineSegment(sketch, "E670", {"start": v(97.94, 9.92) * mm, "end": v(97.31, 9.92) * mm});
            skLineSegment(sketch, "E671", {"start": v(97.31, 9.92) * mm, "end": v(96.73, 9.92) * mm});
            skLineSegment(sketch, "E672", {"start": v(96.73, 9.92) * mm, "end": v(95, 10.37) * mm});
            skLineSegment(sketch, "E673", {"start": v(95, 10.37) * mm, "end": v(93.3, 11.41) * mm});
            skLineSegment(sketch, "E674", {"start": v(93.3, 11.41) * mm, "end": v(93, 11.7) * mm});
            skLineSegment(sketch, "E675", {"start": v(93, 11.7) * mm, "end": v(92.69, 12) * mm});
            skLineSegment(sketch, "E676", {"start": v(92.69, 12) * mm, "end": v(91.6, 13.6) * mm});
            skLineSegment(sketch, "E677", {"start": v(91.6, 13.6) * mm, "end": v(91.14, 15.16) * mm});
            skLineSegment(sketch, "E678", {"start": v(91.14, 15.16) * mm, "end": v(91.14, 15.68) * mm});
            skLineSegment(sketch, "E679", {"start": v(91.14, 15.68) * mm, "end": v(91.13, 15.76) * mm});
            skLineSegment(sketch, "E680", {"start": v(91.13, 15.76) * mm, "end": v(91.1, 16.2) * mm});
            skLineSegment(sketch, "E681", {"start": v(91.1, 16.2) * mm, "end": v(91.1, 16.35) * mm});
            skLineSegment(sketch, "E682", {"start": v(91.1, 16.35) * mm, "end": v(91.1, 16.46) * mm});
            skLineSegment(sketch, "E683", {"start": v(91.1, 16.46) * mm, "end": v(91.2, 16.78) * mm});
            skLineSegment(sketch, "E684", {"start": v(91.2, 16.78) * mm, "end": v(91.21, 16.8) * mm});
            skLineSegment(sketch, "E685", {"start": v(91.21, 16.8) * mm, "end": v(91.23, 16.84) * mm});
            skLineSegment(sketch, "E686", {"start": v(91.23, 16.84) * mm, "end": v(91.64, 17.06) * mm});
            skLineSegment(sketch, "E687", {"start": v(91.64, 17.06) * mm, "end": v(91.7, 17.07) * mm});
            skLineSegment(sketch, "E688", {"start": v(91.7, 17.07) * mm, "end": v(91.76, 17.09) * mm});
            skLineSegment(sketch, "E689", {"start": v(91.76, 17.09) * mm, "end": v(92.13, 17.16) * mm});
            skLineSegment(sketch, "E690", {"start": v(92.13, 17.16) * mm, "end": v(92.25, 17.16) * mm});
            skLineSegment(sketch, "E691", {"start": v(92.25, 17.16) * mm, "end": v(92.4, 17.16) * mm});
            skLineSegment(sketch, "E692", {"start": v(92.4, 17.16) * mm, "end": v(92.83, 16.98) * mm});
            skLineSegment(sketch, "E693", {"start": v(92.83, 16.98) * mm, "end": v(92.86, 16.94) * mm});
            skLineSegment(sketch, "E694", {"start": v(92.86, 16.94) * mm, "end": v(92.9, 16.9) * mm});
            skLineSegment(sketch, "E695", {"start": v(92.9, 16.9) * mm, "end": v(93.15, 16.4) * mm});
            skLineSegment(sketch, "E696", {"start": v(93.15, 16.4) * mm, "end": v(93.17, 16.35) * mm});
            skLineSegment(sketch, "E697", {"start": v(-73.17, 40.98) * mm, "end": v(-74.3, 40.98) * mm});
            skLineSegment(sketch, "E698", {"start": v(-74.3, 40.98) * mm, "end": v(-77.71, 40.46) * mm});
            skLineSegment(sketch, "E699", {"start": v(-77.71, 40.46) * mm, "end": v(-81.88, 38.95) * mm});
            skLineSegment(sketch, "E700", {"start": v(-81.88, 38.95) * mm, "end": v(-85.54, 36.6) * mm});
            skLineSegment(sketch, "E701", {"start": v(-85.54, 36.6) * mm, "end": v(-87.93, 34.36) * mm});
            skLineSegment(sketch, "E702", {"start": v(-87.93, 34.36) * mm, "end": v(-88.6, 33.52) * mm});
            skLineSegment(sketch, "E703", {"start": v(-88.6, 33.52) * mm, "end": v(-88.52, 33.27) * mm});
            skLineSegment(sketch, "E704", {"start": v(-88.52, 33.27) * mm, "end": v(-88.27, 32.54) * mm});
            skLineSegment(sketch, "E705", {"start": v(-88.27, 32.54) * mm, "end": v(-87.76, 31.14) * mm});
            skLineSegment(sketch, "E706", {"start": v(-87.76, 31.14) * mm, "end": v(-87.03, 29.37) * mm});
            skLineSegment(sketch, "E707", {"start": v(-87.03, 29.37) * mm, "end": v(-86.3, 27.8) * mm});
            skLineSegment(sketch, "E708", {"start": v(-86.3, 27.8) * mm, "end": v(-86.05, 27.3) * mm});
            skLineSegment(sketch, "E709", {"start": v(-86.05, 27.3) * mm, "end": v(-86, 27.32) * mm});
            skLineSegment(sketch, "E710", {"start": v(-86, 27.32) * mm, "end": v(-85.46, 27.43) * mm});
            skLineSegment(sketch, "E711", {"start": v(-85.46, 27.43) * mm, "end": v(-85.41, 27.43) * mm});
            skLineSegment(sketch, "E712", {"start": v(-85.41, 27.43) * mm, "end": v(-85.1, 28.44) * mm});
            skLineSegment(sketch, "E713", {"start": v(-85.1, 28.44) * mm, "end": v(-83.59, 31.3) * mm});
            skLineSegment(sketch, "E714", {"start": v(-83.59, 31.3) * mm, "end": v(-81.01, 34.35) * mm});
            skLineSegment(sketch, "E715", {"start": v(-81.01, 34.35) * mm, "end": v(-78.09, 36.58) * mm});
            skLineSegment(sketch, "E716", {"start": v(-78.09, 36.58) * mm, "end": v(-75.96, 37.7) * mm});
            skLineSegment(sketch, "E717", {"start": v(-75.96, 37.7) * mm, "end": v(-75.2, 37.97) * mm});
            skLineSegment(sketch, "E718", {"start": v(-75.2, 37.97) * mm, "end": v(-74.58, 38.2) * mm});
            skLineSegment(sketch, "E719", {"start": v(-74.58, 38.2) * mm, "end": v(-72.65, 38.74) * mm});
            skLineSegment(sketch, "E720", {"start": v(-72.65, 38.74) * mm, "end": v(-70.55, 39.15) * mm});
            skLineSegment(sketch, "E721", {"start": v(-70.55, 39.15) * mm, "end": v(-69, 39.32) * mm});
            skLineSegment(sketch, "E722", {"start": v(-69, 39.32) * mm, "end": v(-68.28, 39.36) * mm});
            skLineSegment(sketch, "E723", {"start": v(-68.28, 39.36) * mm, "end": v(-68.1, 39.37) * mm});
            skLineSegment(sketch, "E724", {"start": v(-68.1, 39.37) * mm, "end": v(-69.15, 39.25) * mm});
            skLineSegment(sketch, "E725", {"start": v(-69.15, 39.25) * mm, "end": v(-74.23, 37.83) * mm});
            skLineSegment(sketch, "E726", {"start": v(-74.23, 37.83) * mm, "end": v(-78.72, 35.3) * mm});
            skLineSegment(sketch, "E727", {"start": v(-78.72, 35.3) * mm, "end": v(-79.47, 34.61) * mm});
            skLineSegment(sketch, "E728", {"start": v(-79.47, 34.61) * mm, "end": v(-80.09, 34.09) * mm});
            skLineSegment(sketch, "E729", {"start": v(-80.09, 34.09) * mm, "end": v(-82.53, 31) * mm});
            skLineSegment(sketch, "E730", {"start": v(-82.53, 31) * mm, "end": v(-84.13, 27.57) * mm});
            skLineSegment(sketch, "E731", {"start": v(-84.13, 27.57) * mm, "end": v(-84.32, 26.86) * mm});
            skLineSegment(sketch, "E732", {"start": v(-84.32, 26.86) * mm, "end": v(-84.3, 26.83) * mm});
            skLineSegment(sketch, "E733", {"start": v(-84.3, 26.83) * mm, "end": v(-84.11, 26.47) * mm});
            skLineSegment(sketch, "E734", {"start": v(-84.11, 26.47) * mm, "end": v(-84.1, 26.43) * mm});
            skLineSegment(sketch, "E735", {"start": v(-84.1, 26.43) * mm, "end": v(-84.05, 26.27) * mm});
            skLineSegment(sketch, "E736", {"start": v(-84.05, 26.27) * mm, "end": v(-84.08, 25.45) * mm});
            skLineSegment(sketch, "E737", {"start": v(-84.08, 25.45) * mm, "end": v(-84.44, 24.7) * mm});
            skLineSegment(sketch, "E738", {"start": v(-84.44, 24.7) * mm, "end": v(-84.55, 24.57) * mm});
            skLineSegment(sketch, "E739", {"start": v(-84.55, 24.57) * mm, "end": v(-84.48, 24.45) * mm});
            skLineSegment(sketch, "E740", {"start": v(-84.48, 24.45) * mm, "end": v(-83.7, 23.18) * mm});
            skLineSegment(sketch, "E741", {"start": v(-83.7, 23.18) * mm, "end": v(-83.6, 23.05) * mm});
            skLineSegment(sketch, "E742", {"start": v(-83.6, 23.05) * mm, "end": v(-82.99, 22.09) * mm});
            skLineSegment(sketch, "E743", {"start": v(-82.99, 22.09) * mm, "end": v(-79.04, 17.1) * mm});
            skLineSegment(sketch, "E744", {"start": v(-79.04, 17.1) * mm, "end": v(-74.05, 12.07) * mm});
            skLineSegment(sketch, "E745", {"start": v(-74.05, 12.07) * mm, "end": v(-72.91, 11.09) * mm});
            skLineSegment(sketch, "E746", {"start": v(-72.91, 11.09) * mm, "end": v(-72.87, 11.15) * mm});
            skLineSegment(sketch, "E747", {"start": v(-72.87, 11.15) * mm, "end": v(-72.26, 11.6) * mm});
            skLineSegment(sketch, "E748", {"start": v(-72.26, 11.6) * mm, "end": v(-72.2, 11.63) * mm});
            skLineSegment(sketch, "E749", {"start": v(-72.2, 11.63) * mm, "end": v(-72.2, 11.78) * mm});
            skLineSegment(sketch, "E750", {"start": v(-72.2, 11.78) * mm, "end": v(-72.32, 13.32) * mm});
            skLineSegment(sketch, "E751", {"start": v(-72.32, 13.32) * mm, "end": v(-72.33, 13.48) * mm});
            skLineSegment(sketch, "E752", {"start": v(-72.33, 13.48) * mm, "end": v(-72.37, 14.34) * mm});
            skLineSegment(sketch, "E753", {"start": v(-72.37, 14.34) * mm, "end": v(-72.2, 16.92) * mm});
            skLineSegment(sketch, "E754", {"start": v(-72.2, 16.92) * mm, "end": v(-71.44, 20.62) * mm});
            skLineSegment(sketch, "E755", {"start": v(-71.44, 20.62) * mm, "end": v(-70.07, 24.42) * mm});
            skLineSegment(sketch, "E756", {"start": v(-70.07, 24.42) * mm, "end": v(-68.64, 27.25) * mm});
            skLineSegment(sketch, "E757", {"start": v(-68.64, 27.25) * mm, "end": v(-68.08, 28.14) * mm});
            skLineSegment(sketch, "E758", {"start": v(-68.08, 28.14) * mm, "end": v(-68.14, 28.22) * mm});
            skLineSegment(sketch, "E759", {"start": v(-68.14, 28.22) * mm, "end": v(-68.45, 29) * mm});
            skLineSegment(sketch, "E760", {"start": v(-68.45, 29) * mm, "end": v(-68.45, 29.27) * mm});
            skLineSegment(sketch, "E761", {"start": v(-68.45, 29.27) * mm, "end": v(-68.45, 29.46) * mm});
            skLineSegment(sketch, "E762", {"start": v(-68.45, 29.46) * mm, "end": v(-68.3, 30.03) * mm});
            skLineSegment(sketch, "E763", {"start": v(-68.3, 30.03) * mm, "end": v(-67.96, 30.56) * mm});
            skLineSegment(sketch, "E764", {"start": v(-67.96, 30.56) * mm, "end": v(-67.87, 30.65) * mm});
            skLineSegment(sketch, "E765", {"start": v(-67.87, 30.65) * mm, "end": v(-68.23, 31) * mm});
            skLineSegment(sketch, "E766", {"start": v(-68.23, 31) * mm, "end": v(-72.05, 34.14) * mm});
            skLineSegment(sketch, "E767", {"start": v(-72.05, 34.14) * mm, "end": v(-72.46, 34.42) * mm});
            skLineSegment(sketch, "E768", {"start": v(-72.46, 34.42) * mm, "end": v(-72.36, 34.37) * mm});
            skLineSegment(sketch, "E769", {"start": v(-72.36, 34.37) * mm, "end": v(-71.87, 34.12) * mm});
            skLineSegment(sketch, "E770", {"start": v(-71.87, 34.12) * mm, "end": v(-70.75, 33.49) * mm});
            skLineSegment(sketch, "E771", {"start": v(-70.75, 33.49) * mm, "end": v(-69.18, 32.48) * mm});
            skLineSegment(sketch, "E772", {"start": v(-69.18, 32.48) * mm, "end": v(-67.75, 31.41) * mm});
            skLineSegment(sketch, "E773", {"start": v(-67.75, 31.41) * mm, "end": v(-67.3, 31.03) * mm});
            skLineSegment(sketch, "E774", {"start": v(-67.3, 31.03) * mm, "end": v(-67.24, 31.06) * mm});
            skLineSegment(sketch, "E775", {"start": v(-67.24, 31.06) * mm, "end": v(-66.7, 31.2) * mm});
            skLineSegment(sketch, "E776", {"start": v(-66.7, 31.2) * mm, "end": v(-66.52, 31.2) * mm});
            skLineSegment(sketch, "E777", {"start": v(-66.52, 31.2) * mm, "end": v(-66.37, 31.2) * mm});
            skLineSegment(sketch, "E778", {"start": v(-66.37, 31.2) * mm, "end": v(-65.96, 31.1) * mm});
            skLineSegment(sketch, "E779", {"start": v(-65.96, 31.1) * mm, "end": v(-65.91, 31.1) * mm});
            skLineSegment(sketch, "E780", {"start": v(-65.91, 31.1) * mm, "end": v(-65.6, 31.46) * mm});
            skLineSegment(sketch, "E781", {"start": v(-65.6, 31.46) * mm, "end": v(-63.95, 33.19) * mm});
            skLineSegment(sketch, "E782", {"start": v(-63.95, 33.19) * mm, "end": v(-62.1, 34.76) * mm});
            skLineSegment(sketch, "E783", {"start": v(-62.1, 34.76) * mm, "end": v(-61.7, 35.05) * mm});
            skLineSegment(sketch, "E784", {"start": v(-61.7, 35.05) * mm, "end": v(-62.02, 34.7) * mm});
            skLineSegment(sketch, "E785", {"start": v(-62.02, 34.7) * mm, "end": v(-64.84, 30.96) * mm});
            skLineSegment(sketch, "E786", {"start": v(-64.84, 30.96) * mm, "end": v(-65.1, 30.56) * mm});
            skLineSegment(sketch, "E787", {"start": v(-65.1, 30.56) * mm, "end": v(-65.02, 30.47) * mm});
            skLineSegment(sketch, "E788", {"start": v(-65.02, 30.47) * mm, "end": v(-64.73, 29.97) * mm});
            skLineSegment(sketch, "E789", {"start": v(-64.73, 29.97) * mm, "end": v(-64.59, 29.44) * mm});
            skLineSegment(sketch, "E790", {"start": v(-64.59, 29.44) * mm, "end": v(-64.59, 29.27) * mm});
            skLineSegment(sketch, "E791", {"start": v(-64.59, 29.27) * mm, "end": v(-64.59, 29.1) * mm});
            skLineSegment(sketch, "E792", {"start": v(-64.59, 29.1) * mm, "end": v(-64.7, 28.66) * mm});
            skLineSegment(sketch, "E793", {"start": v(-64.7, 28.66) * mm, "end": v(-64.71, 28.61) * mm});
            skLineSegment(sketch, "E794", {"start": v(-64.71, 28.61) * mm, "end": v(-64.7, 28.6) * mm});
            skLineSegment(sketch, "E795", {"start": v(-64.7, 28.6) * mm, "end": v(-64.59, 28.49) * mm});
            skLineSegment(sketch, "E796", {"start": v(-64.59, 28.49) * mm, "end": v(-64.58, 28.47) * mm});
            skLineSegment(sketch, "E797", {"start": v(-64.58, 28.47) * mm, "end": v(-63.95, 27.83) * mm});
            skLineSegment(sketch, "E798", {"start": v(-63.95, 27.83) * mm, "end": v(-62.29, 25.66) * mm});
            skLineSegment(sketch, "E799", {"start": v(-62.29, 25.66) * mm, "end": v(-60.26, 22.14) * mm});
            skLineSegment(sketch, "E800", {"start": v(-60.26, 22.14) * mm, "end": v(-58.7, 18.1) * mm});
            skLineSegment(sketch, "E801", {"start": v(-58.7, 18.1) * mm, "end": v(-57.95, 14.8) * mm});
            skLineSegment(sketch, "E802", {"start": v(-57.95, 14.8) * mm, "end": v(-57.84, 13.7) * mm});
            skLineSegment(sketch, "E803", {"start": v(-57.84, 13.7) * mm, "end": v(-57.78, 13.72) * mm});
            skLineSegment(sketch, "E804", {"start": v(-57.78, 13.72) * mm, "end": v(-57.17, 13.87) * mm});
            skLineSegment(sketch, "E805", {"start": v(-57.17, 13.87) * mm, "end": v(-57.11, 13.86) * mm});
            skLineSegment(sketch, "E806", {"start": v(-57.11, 13.86) * mm, "end": v(-57, 13.86) * mm});
            skLineSegment(sketch, "E807", {"start": v(-57, 13.86) * mm, "end": v(-56.6, 13.67) * mm});
            skLineSegment(sketch, "E808", {"start": v(-56.6, 13.67) * mm, "end": v(-56.42, 13.29) * mm});
            skLineSegment(sketch, "E809", {"start": v(-56.42, 13.29) * mm, "end": v(-56.42, 13.18) * mm});
            skLineSegment(sketch, "E810", {"start": v(-56.42, 13.18) * mm, "end": v(-56.32, 13.23) * mm});
            skLineSegment(sketch, "E811", {"start": v(-56.32, 13.23) * mm, "end": v(-55.32, 13.73) * mm});
            skLineSegment(sketch, "E812", {"start": v(-55.32, 13.73) * mm, "end": v(-55.22, 13.78) * mm});
            skLineSegment(sketch, "E813", {"start": v(-55.22, 13.78) * mm, "end": v(-55.5, 13.54) * mm});
            skLineSegment(sketch, "E814", {"start": v(-55.5, 13.54) * mm, "end": v(-56.24, 13.03) * mm});
            skLineSegment(sketch, "E815", {"start": v(-56.24, 13.03) * mm, "end": v(-56.44, 12.9) * mm});
            skLineSegment(sketch, "E816", {"start": v(-56.44, 12.9) * mm, "end": v(-56.46, 12.84) * mm});
            skLineSegment(sketch, "E817", {"start": v(-56.46, 12.84) * mm, "end": v(-56.7, 12.26) * mm});
            skLineSegment(sketch, "E818", {"start": v(-56.7, 12.26) * mm, "end": v(-56.73, 12.2) * mm});
            skLineSegment(sketch, "E819", {"start": v(-56.73, 12.2) * mm, "end": v(-56.8, 12.1) * mm});
            skLineSegment(sketch, "E820", {"start": v(-56.8, 12.1) * mm, "end": v(-57.65, 11.18) * mm});
            skLineSegment(sketch, "E821", {"start": v(-57.65, 11.18) * mm, "end": v(-57.75, 11.1) * mm});
            skLineSegment(sketch, "E822", {"start": v(-57.75, 11.1) * mm, "end": v(-57.75, 10.92) * mm});
            skLineSegment(sketch, "E823", {"start": v(-57.75, 10.92) * mm, "end": v(-57.9, 9.03) * mm});
            skLineSegment(sketch, "E824", {"start": v(-57.9, 9.03) * mm, "end": v(-57.93, 8.84) * mm});
            skLineSegment(sketch, "E825", {"start": v(-57.93, 8.84) * mm, "end": v(-57.42, 9.47) * mm});
            skLineSegment(sketch, "E826", {"start": v(-57.42, 9.47) * mm, "end": v(-56.07, 11.55) * mm});
            skLineSegment(sketch, "E827", {"start": v(-56.07, 11.55) * mm, "end": v(-54.67, 14.57) * mm});
            skLineSegment(sketch, "E828", {"start": v(-54.67, 14.57) * mm, "end": v(-53.8, 17.84) * mm});
            skLineSegment(sketch, "E829", {"start": v(-53.8, 17.84) * mm, "end": v(-53.49, 20.44) * mm});
            skLineSegment(sketch, "E830", {"start": v(-53.49, 20.44) * mm, "end": v(-53.49, 21.3) * mm});
            skLineSegment(sketch, "E831", {"start": v(-53.49, 21.3) * mm, "end": v(-53.49, 22.3) * mm});
            skLineSegment(sketch, "E832", {"start": v(-53.49, 22.3) * mm, "end": v(-53.89, 25.27) * mm});
            skLineSegment(sketch, "E833", {"start": v(-53.89, 25.27) * mm, "end": v(-55.03, 28.96) * mm});
            skLineSegment(sketch, "E834", {"start": v(-55.03, 28.96) * mm, "end": v(-56.85, 32.3) * mm});
            skLineSegment(sketch, "E835", {"start": v(-56.85, 32.3) * mm, "end": v(-59.25, 35.22) * mm});
            skLineSegment(sketch, "E836", {"start": v(-59.25, 35.22) * mm, "end": v(-62.17, 37.62) * mm});
            skLineSegment(sketch, "E837", {"start": v(-62.17, 37.62) * mm, "end": v(-65.5, 39.44) * mm});
            skLineSegment(sketch, "E838", {"start": v(-65.5, 39.44) * mm, "end": v(-69.2, 40.58) * mm});
            skLineSegment(sketch, "E839", {"start": v(-69.2, 40.58) * mm, "end": v(-72.18, 40.98) * mm});
            skLineSegment(sketch, "E840", {"start": v(-72.18, 40.98) * mm, "end": v(-73.17, 40.98) * mm});
            skLineSegment(sketch, "E841", {"start": v(-59.1, 10.57) * mm, "end": v(-59.22, 10.58) * mm});
            skLineSegment(sketch, "E842", {"start": v(-59.22, 10.58) * mm, "end": v(-59.63, 10.77) * mm});
            skLineSegment(sketch, "E843", {"start": v(-59.63, 10.77) * mm, "end": v(-59.8, 11.19) * mm});
            skLineSegment(sketch, "E844", {"start": v(-59.8, 11.19) * mm, "end": v(-59.8, 11.3) * mm});
            skLineSegment(sketch, "E845", {"start": v(-59.8, 11.3) * mm, "end": v(-60.07, 11.2) * mm});
            skLineSegment(sketch, "E846", {"start": v(-60.07, 11.2) * mm, "end": v(-61.58, 10.73) * mm});
            skLineSegment(sketch, "E847", {"start": v(-61.58, 10.73) * mm, "end": v(-63.28, 10.34) * mm});
            skLineSegment(sketch, "E848", {"start": v(-63.28, 10.34) * mm, "end": v(-63.65, 10.27) * mm});
            skLineSegment(sketch, "E849", {"start": v(-63.65, 10.27) * mm, "end": v(-64.14, 10.18) * mm});
            skLineSegment(sketch, "E850", {"start": v(-64.14, 10.18) * mm, "end": v(-66.77, 9.83) * mm});
            skLineSegment(sketch, "E851", {"start": v(-66.77, 9.83) * mm, "end": v(-69.62, 9.65) * mm});
            skLineSegment(sketch, "E852", {"start": v(-69.62, 9.65) * mm, "end": v(-70.22, 9.64) * mm});
            skLineSegment(sketch, "E853", {"start": v(-70.22, 9.64) * mm, "end": v(-70.24, 9.6) * mm});
            skLineSegment(sketch, "E854", {"start": v(-70.24, 9.6) * mm, "end": v(-70.54, 9.2) * mm});
            skLineSegment(sketch, "E855", {"start": v(-70.54, 9.2) * mm, "end": v(-70.58, 9.16) * mm});
            skLineSegment(sketch, "E856", {"start": v(-70.58, 9.16) * mm, "end": v(-70.06, 8.75) * mm});
            skLineSegment(sketch, "E857", {"start": v(-70.06, 8.75) * mm, "end": v(-64.5, 4.82) * mm});
            skLineSegment(sketch, "E858", {"start": v(-64.5, 4.82) * mm, "end": v(-63.91, 4.45) * mm});
            skLineSegment(sketch, "E859", {"start": v(-63.91, 4.45) * mm, "end": v(-64.5, 4.73) * mm});
            skLineSegment(sketch, "E860", {"start": v(-64.5, 4.73) * mm, "end": v(-67.36, 6.24) * mm});
            skLineSegment(sketch, "E861", {"start": v(-67.36, 6.24) * mm, "end": v(-70.15, 7.94) * mm});
            skLineSegment(sketch, "E862", {"start": v(-70.15, 7.94) * mm, "end": v(-70.7, 8.3) * mm});
            skLineSegment(sketch, "E863", {"start": v(-70.7, 8.3) * mm, "end": v(-70.63, 7.86) * mm});
            skLineSegment(sketch, "E864", {"start": v(-70.63, 7.86) * mm, "end": v(-69.62, 3.5) * mm});
            skLineSegment(sketch, "E865", {"start": v(-69.62, 3.5) * mm, "end": v(-69.47, 3.07) * mm});
            skLineSegment(sketch, "E866", {"start": v(-69.47, 3.07) * mm, "end": v(-69.51, 3.16) * mm});
            skLineSegment(sketch, "E867", {"start": v(-69.51, 3.16) * mm, "end": v(-69.78, 3.63) * mm});
            skLineSegment(sketch, "E868", {"start": v(-69.78, 3.63) * mm, "end": v(-70.35, 4.75) * mm});
            skLineSegment(sketch, "E869", {"start": v(-70.35, 4.75) * mm, "end": v(-71.03, 6.41) * mm});
            skLineSegment(sketch, "E870", {"start": v(-71.03, 6.41) * mm, "end": v(-71.54, 8.06) * mm});
            skLineSegment(sketch, "E871", {"start": v(-71.54, 8.06) * mm, "end": v(-71.68, 8.62) * mm});
            skLineSegment(sketch, "E872", {"start": v(-71.68, 8.62) * mm, "end": v(-71.7, 8.61) * mm});
            skLineSegment(sketch, "E873", {"start": v(-71.7, 8.61) * mm, "end": v(-71.85, 8.6) * mm});
            skLineSegment(sketch, "E874", {"start": v(-71.85, 8.6) * mm, "end": v(-71.9, 8.6) * mm});
            skLineSegment(sketch, "E875", {"start": v(-71.9, 8.6) * mm, "end": v(-72.14, 8.6) * mm});
            skLineSegment(sketch, "E876", {"start": v(-72.14, 8.6) * mm, "end": v(-72.83, 8.9) * mm});
            skLineSegment(sketch, "E877", {"start": v(-72.83, 8.9) * mm, "end": v(-73.27, 9.54) * mm});
            skLineSegment(sketch, "E878", {"start": v(-73.27, 9.54) * mm, "end": v(-73.3, 9.7) * mm});
            skLineSegment(sketch, "E879", {"start": v(-73.3, 9.7) * mm, "end": v(-74.2, 9.75) * mm});
            skLineSegment(sketch, "E880", {"start": v(-74.2, 9.75) * mm, "end": v(-78.77, 10.33) * mm});
            skLineSegment(sketch, "E881", {"start": v(-78.77, 10.33) * mm, "end": v(-83.42, 11.38) * mm});
            skLineSegment(sketch, "E882", {"start": v(-83.42, 11.38) * mm, "end": v(-84.34, 11.67) * mm});
            skLineSegment(sketch, "E883", {"start": v(-84.34, 11.67) * mm, "end": v(-83.5, 11.55) * mm});
            skLineSegment(sketch, "E884", {"start": v(-83.5, 11.55) * mm, "end": v(-74.96, 10.84) * mm});
            skLineSegment(sketch, "E885", {"start": v(-74.96, 10.84) * mm, "end": v(-74.1, 10.81) * mm});
            skLineSegment(sketch, "E886", {"start": v(-74.1, 10.81) * mm, "end": v(-75.24, 11.73) * mm});
            skLineSegment(sketch, "E887", {"start": v(-75.24, 11.73) * mm, "end": v(-80.38, 16.9) * mm});
            skLineSegment(sketch, "E888", {"start": v(-80.38, 16.9) * mm, "end": v(-84.6, 22.8) * mm});
            skLineSegment(sketch, "E889", {"start": v(-84.6, 22.8) * mm, "end": v(-85.28, 24.1) * mm});
            skLineSegment(sketch, "E890", {"start": v(-85.28, 24.1) * mm, "end": v(-85.42, 24.05) * mm});
            skLineSegment(sketch, "E891", {"start": v(-85.42, 24.05) * mm, "end": v(-85.86, 24) * mm});
            skLineSegment(sketch, "E892", {"start": v(-85.86, 24) * mm, "end": v(-86.4, 24.14) * mm});
            skLineSegment(sketch, "E893", {"start": v(-86.4, 24.14) * mm, "end": v(-86.83, 24.48) * mm});
            skLineSegment(sketch, "E894", {"start": v(-86.83, 24.48) * mm, "end": v(-87.06, 24.87) * mm});
            skLineSegment(sketch, "E895", {"start": v(-87.06, 24.87) * mm, "end": v(-87.1, 25) * mm});
            skLineSegment(sketch, "E896", {"start": v(-87.1, 25) * mm, "end": v(-87.16, 25.17) * mm});
            skLineSegment(sketch, "E897", {"start": v(-87.16, 25.17) * mm, "end": v(-87.12, 26.01) * mm});
            skLineSegment(sketch, "E898", {"start": v(-87.12, 26.01) * mm, "end": v(-86.74, 26.77) * mm});
            skLineSegment(sketch, "E899", {"start": v(-86.74, 26.77) * mm, "end": v(-86.62, 26.9) * mm});
            skLineSegment(sketch, "E900", {"start": v(-86.62, 26.9) * mm, "end": v(-86.84, 27.42) * mm});
            skLineSegment(sketch, "E901", {"start": v(-86.84, 27.42) * mm, "end": v(-87.8, 30.1) * mm});
            skLineSegment(sketch, "E902", {"start": v(-87.8, 30.1) * mm, "end": v(-88.55, 32.86) * mm});
            skLineSegment(sketch, "E903", {"start": v(-88.55, 32.86) * mm, "end": v(-88.67, 33.43) * mm});
            skLineSegment(sketch, "E904", {"start": v(-88.67, 33.43) * mm, "end": v(-89.16, 32.8) * mm});
            skLineSegment(sketch, "E905", {"start": v(-89.16, 32.8) * mm, "end": v(-90.43, 30.77) * mm});
            skLineSegment(sketch, "E906", {"start": v(-90.43, 30.77) * mm, "end": v(-91.74, 27.83) * mm});
            skLineSegment(sketch, "E907", {"start": v(-91.74, 27.83) * mm, "end": v(-92.57, 24.66) * mm});
            skLineSegment(sketch, "E908", {"start": v(-92.57, 24.66) * mm, "end": v(-92.85, 22.14) * mm});
            skLineSegment(sketch, "E909", {"start": v(-92.85, 22.14) * mm, "end": v(-92.85, 21.3) * mm});
            skLineSegment(sketch, "E910", {"start": v(-92.85, 21.3) * mm, "end": v(-92.85, 20.31) * mm});
            skLineSegment(sketch, "E911", {"start": v(-92.85, 20.31) * mm, "end": v(-92.46, 17.34) * mm});
            skLineSegment(sketch, "E912", {"start": v(-92.46, 17.34) * mm, "end": v(-91.3, 13.64) * mm});
            skLineSegment(sketch, "E913", {"start": v(-91.3, 13.64) * mm, "end": v(-89.5, 10.3) * mm});
            skLineSegment(sketch, "E914", {"start": v(-89.5, 10.3) * mm, "end": v(-87.09, 7.38) * mm});
            skLineSegment(sketch, "E915", {"start": v(-87.09, 7.38) * mm, "end": v(-84.18, 4.98) * mm});
            skLineSegment(sketch, "E916", {"start": v(-84.18, 4.98) * mm, "end": v(-80.83, 3.17) * mm});
            skLineSegment(sketch, "E917", {"start": v(-80.83, 3.17) * mm, "end": v(-77.14, 2.02) * mm});
            skLineSegment(sketch, "E918", {"start": v(-77.14, 2.02) * mm, "end": v(-74.16, 1.62) * mm});
            skLineSegment(sketch, "E919", {"start": v(-74.16, 1.62) * mm, "end": v(-73.17, 1.62) * mm});
            skLineSegment(sketch, "E920", {"start": v(-73.17, 1.62) * mm, "end": v(-72.07, 1.62) * mm});
            skLineSegment(sketch, "E921", {"start": v(-72.07, 1.62) * mm, "end": v(-68.78, 2.1) * mm});
            skLineSegment(sketch, "E922", {"start": v(-68.78, 2.1) * mm, "end": v(-64.74, 3.51) * mm});
            skLineSegment(sketch, "E923", {"start": v(-64.74, 3.51) * mm, "end": v(-61.15, 5.72) * mm});
            skLineSegment(sketch, "E924", {"start": v(-61.15, 5.72) * mm, "end": v(-58.8, 7.82) * mm});
            skLineSegment(sketch, "E925", {"start": v(-58.8, 7.82) * mm, "end": v(-58.13, 8.61) * mm});
            skLineSegment(sketch, "E926", {"start": v(-58.13, 8.61) * mm, "end": v(-58.13, 8.8) * mm});
            skLineSegment(sketch, "E927", {"start": v(-58.13, 8.8) * mm, "end": v(-58.2, 10.64) * mm});
            skLineSegment(sketch, "E928", {"start": v(-58.2, 10.64) * mm, "end": v(-58.21, 10.82) * mm});
            skLineSegment(sketch, "E929", {"start": v(-58.21, 10.82) * mm, "end": v(-58.3, 10.78) * mm});
            skLineSegment(sketch, "E930", {"start": v(-58.3, 10.78) * mm, "end": v(-59.03, 10.57) * mm});
            skLineSegment(sketch, "E931", {"start": v(-59.03, 10.57) * mm, "end": v(-59.1, 10.57) * mm});
            skLineSegment(sketch, "E932", {"start": v(-70.06, 10.79) * mm, "end": v(-70.01, 10.79) * mm});
            skLineSegment(sketch, "E933", {"start": v(-70.01, 10.79) * mm, "end": v(-69.53, 10.8) * mm});
            skLineSegment(sketch, "E934", {"start": v(-69.53, 10.8) * mm, "end": v(-69.48, 10.8) * mm});
            skLineSegment(sketch, "E935", {"start": v(-69.48, 10.8) * mm, "end": v(-68.66, 10.82) * mm});
            skLineSegment(sketch, "E936", {"start": v(-68.66, 10.82) * mm, "end": v(-64.48, 11.14) * mm});
            skLineSegment(sketch, "E937", {"start": v(-64.48, 11.14) * mm, "end": v(-60.37, 11.83) * mm});
            skLineSegment(sketch, "E938", {"start": v(-60.37, 11.83) * mm, "end": v(-59.58, 12.04) * mm});
            skLineSegment(sketch, "E939", {"start": v(-59.58, 12.04) * mm, "end": v(-59.57, 12.06) * mm});
            skLineSegment(sketch, "E940", {"start": v(-59.57, 12.06) * mm, "end": v(-59.48, 12.22) * mm});
            skLineSegment(sketch, "E941", {"start": v(-59.48, 12.22) * mm, "end": v(-59.48, 12.24) * mm});
            skLineSegment(sketch, "E942", {"start": v(-59.48, 12.24) * mm, "end": v(-59.41, 12.34) * mm});
            skLineSegment(sketch, "E943", {"start": v(-59.41, 12.34) * mm, "end": v(-58.61, 13.21) * mm});
            skLineSegment(sketch, "E944", {"start": v(-58.61, 13.21) * mm, "end": v(-58.52, 13.28) * mm});
            skLineSegment(sketch, "E945", {"start": v(-58.52, 13.28) * mm, "end": v(-58.7, 14.27) * mm});
            skLineSegment(sketch, "E946", {"start": v(-58.7, 14.27) * mm, "end": v(-59.48, 17.19) * mm});
            skLineSegment(sketch, "E947", {"start": v(-59.48, 17.19) * mm, "end": v(-60.95, 20.94) * mm});
            skLineSegment(sketch, "E948", {"start": v(-60.95, 20.94) * mm, "end": v(-62.9, 24.5) * mm});
            skLineSegment(sketch, "E949", {"start": v(-62.9, 24.5) * mm, "end": v(-64.64, 27.01) * mm});
            skLineSegment(sketch, "E950", {"start": v(-64.64, 27.01) * mm, "end": v(-65.28, 27.8) * mm});
            skLineSegment(sketch, "E951", {"start": v(-65.28, 27.8) * mm, "end": v(-65.36, 27.73) * mm});
            skLineSegment(sketch, "E952", {"start": v(-65.36, 27.73) * mm, "end": v(-66.23, 27.33) * mm});
            skLineSegment(sketch, "E953", {"start": v(-66.23, 27.33) * mm, "end": v(-66.52, 27.33) * mm});
            skLineSegment(sketch, "E954", {"start": v(-66.52, 27.33) * mm, "end": v(-66.62, 27.33) * mm});
            skLineSegment(sketch, "E955", {"start": v(-66.62, 27.33) * mm, "end": v(-66.9, 27.37) * mm});
            skLineSegment(sketch, "E956", {"start": v(-66.9, 27.37) * mm, "end": v(-66.94, 27.38) * mm});
            skLineSegment(sketch, "E957", {"start": v(-66.94, 27.38) * mm, "end": v(-67.57, 26.17) * mm});
            skLineSegment(sketch, "E958", {"start": v(-67.57, 26.17) * mm, "end": v(-69.88, 19.74) * mm});
            skLineSegment(sketch, "E959", {"start": v(-69.88, 19.74) * mm, "end": v(-70.92, 13.06) * mm});
            skLineSegment(sketch, "E960", {"start": v(-70.92, 13.06) * mm, "end": v(-70.91, 11.7) * mm});
            skLineSegment(sketch, "E961", {"start": v(-70.91, 11.7) * mm, "end": v(-70.8, 11.67) * mm});
            skLineSegment(sketch, "E962", {"start": v(-70.8, 11.67) * mm, "end": v(-70.37, 11.35) * mm});
            skLineSegment(sketch, "E963", {"start": v(-70.37, 11.35) * mm, "end": v(-70.09, 10.9) * mm});
            skLineSegment(sketch, "E964", {"start": v(-70.09, 10.9) * mm, "end": v(-70.06, 10.79) * mm});
            skLineSegment(sketch, "E965", {"start": v(-71.9, 43.6) * mm, "end": v(-73.03, 43.6) * mm});
            skLineSegment(sketch, "E966", {"start": v(-73.03, 43.6) * mm, "end": v(-76.43, 43.16) * mm});
            skLineSegment(sketch, "E967", {"start": v(-76.43, 43.16) * mm, "end": v(-80.66, 41.87) * mm});
            skLineSegment(sketch, "E968", {"start": v(-80.66, 41.87) * mm, "end": v(-84.49, 39.84) * mm});
            skLineSegment(sketch, "E969", {"start": v(-84.49, 39.84) * mm, "end": v(-87.82, 37.14) * mm});
            skLineSegment(sketch, "E970", {"start": v(-87.82, 37.14) * mm, "end": v(-90.57, 33.87) * mm});
            skLineSegment(sketch, "E971", {"start": v(-90.57, 33.87) * mm, "end": v(-92.65, 30.12) * mm});
            skLineSegment(sketch, "E972", {"start": v(-92.65, 30.12) * mm, "end": v(-93.96, 25.97) * mm});
            skLineSegment(sketch, "E973", {"start": v(-93.96, 25.97) * mm, "end": v(-94.42, 22.63) * mm});
            skLineSegment(sketch, "E974", {"start": v(-94.42, 22.63) * mm, "end": v(-94.42, 21.52) * mm});
            skLineSegment(sketch, "E975", {"start": v(-94.42, 21.52) * mm, "end": v(-94.42, 20.4) * mm});
            skLineSegment(sketch, "E976", {"start": v(-94.42, 20.4) * mm, "end": v(-93.96, 17.07) * mm});
            skLineSegment(sketch, "E977", {"start": v(-93.96, 17.07) * mm, "end": v(-92.65, 12.92) * mm});
            skLineSegment(sketch, "E978", {"start": v(-92.65, 12.92) * mm, "end": v(-90.57, 9.17) * mm});
            skLineSegment(sketch, "E979", {"start": v(-90.57, 9.17) * mm, "end": v(-87.82, 5.9) * mm});
            skLineSegment(sketch, "E980", {"start": v(-87.82, 5.9) * mm, "end": v(-84.49, 3.2) * mm});
            skLineSegment(sketch, "E981", {"start": v(-84.49, 3.2) * mm, "end": v(-80.66, 1.17) * mm});
            skLineSegment(sketch, "E982", {"start": v(-80.66, 1.17) * mm, "end": v(-76.43, -0.12) * mm});
            skLineSegment(sketch, "E983", {"start": v(-76.43, -0.12) * mm, "end": v(-73.03, -0.57) * mm});
            skLineSegment(sketch, "E984", {"start": v(-73.03, -0.57) * mm, "end": v(-71.9, -0.57) * mm});
            skLineSegment(sketch, "E985", {"start": v(-71.9, -0.57) * mm, "end": v(-70.76, -0.57) * mm});
            skLineSegment(sketch, "E986", {"start": v(-70.76, -0.57) * mm, "end": v(-67.35, -0.12) * mm});
            skLineSegment(sketch, "E987", {"start": v(-67.35, -0.12) * mm, "end": v(-63.12, 1.17) * mm});
            skLineSegment(sketch, "E988", {"start": v(-63.12, 1.17) * mm, "end": v(-59.3, 3.2) * mm});
            skLineSegment(sketch, "E989", {"start": v(-59.3, 3.2) * mm, "end": v(-55.96, 5.9) * mm});
            skLineSegment(sketch, "E990", {"start": v(-55.96, 5.9) * mm, "end": v(-53.21, 9.17) * mm});
            skLineSegment(sketch, "E991", {"start": v(-53.21, 9.17) * mm, "end": v(-51.14, 12.92) * mm});
            skLineSegment(sketch, "E992", {"start": v(-51.14, 12.92) * mm, "end": v(-49.82, 17.07) * mm});
            skLineSegment(sketch, "E993", {"start": v(-49.82, 17.07) * mm, "end": v(-49.37, 20.4) * mm});
            skLineSegment(sketch, "E994", {"start": v(-49.37, 20.4) * mm, "end": v(-49.37, 21.52) * mm});
            skLineSegment(sketch, "E995", {"start": v(-49.37, 21.52) * mm, "end": v(-49.37, 22.63) * mm});
            skLineSegment(sketch, "E996", {"start": v(-49.37, 22.63) * mm, "end": v(-49.82, 25.97) * mm});
            skLineSegment(sketch, "E997", {"start": v(-49.82, 25.97) * mm, "end": v(-51.14, 30.12) * mm});
            skLineSegment(sketch, "E998", {"start": v(-51.14, 30.12) * mm, "end": v(-53.21, 33.87) * mm});
            skLineSegment(sketch, "E999", {"start": v(-53.21, 33.87) * mm, "end": v(-55.96, 37.14) * mm});
            skLineSegment(sketch, "E1000", {"start": v(-55.96, 37.14) * mm, "end": v(-59.3, 39.84) * mm});
            skLineSegment(sketch, "E1001", {"start": v(-59.3, 39.84) * mm, "end": v(-63.12, 41.87) * mm});
            skLineSegment(sketch, "E1002", {"start": v(-63.12, 41.87) * mm, "end": v(-67.35, 43.16) * mm});
            skLineSegment(sketch, "E1003", {"start": v(-67.35, 43.16) * mm, "end": v(-70.76, 43.6) * mm});
            skLineSegment(sketch, "E1004", {"start": v(-70.76, 43.6) * mm, "end": v(-71.9, 43.6) * mm});
            skLineSegment(sketch, "E1005", {"start": v(-72.33, 0.52) * mm, "end": v(-73.4, 0.52) * mm});
            skLineSegment(sketch, "E1006", {"start": v(-73.4, 0.52) * mm, "end": v(-76.65, 0.95) * mm});
            skLineSegment(sketch, "E1007", {"start": v(-76.65, 0.95) * mm, "end": v(-80.67, 2.16) * mm});
            skLineSegment(sketch, "E1008", {"start": v(-80.67, 2.16) * mm, "end": v(-84.31, 4.07) * mm});
            skLineSegment(sketch, "E1009", {"start": v(-84.31, 4.07) * mm, "end": v(-87.48, 6.61) * mm});
            skLineSegment(sketch, "E1010", {"start": v(-87.48, 6.61) * mm, "end": v(-90.1, 9.69) * mm});
            skLineSegment(sketch, "E1011", {"start": v(-90.1, 9.69) * mm, "end": v(-92.08, 13.22) * mm});
            skLineSegment(sketch, "E1012", {"start": v(-92.08, 13.22) * mm, "end": v(-93.33, 17.12) * mm});
            skLineSegment(sketch, "E1013", {"start": v(-93.33, 17.12) * mm, "end": v(-93.76, 20.26) * mm});
            skLineSegment(sketch, "E1014", {"start": v(-93.76, 20.26) * mm, "end": v(-93.76, 21.3) * mm});
            skLineSegment(sketch, "E1015", {"start": v(-93.76, 21.3) * mm, "end": v(-93.76, 22.35) * mm});
            skLineSegment(sketch, "E1016", {"start": v(-93.76, 22.35) * mm, "end": v(-93.33, 25.5) * mm});
            skLineSegment(sketch, "E1017", {"start": v(-93.33, 25.5) * mm, "end": v(-92.08, 29.39) * mm});
            skLineSegment(sketch, "E1018", {"start": v(-92.08, 29.39) * mm, "end": v(-90.1, 32.92) * mm});
            skLineSegment(sketch, "E1019", {"start": v(-90.1, 32.92) * mm, "end": v(-87.48, 36) * mm});
            skLineSegment(sketch, "E1020", {"start": v(-87.48, 36) * mm, "end": v(-84.31, 38.53) * mm});
            skLineSegment(sketch, "E1021", {"start": v(-84.31, 38.53) * mm, "end": v(-80.67, 40.45) * mm});
            skLineSegment(sketch, "E1022", {"start": v(-80.67, 40.45) * mm, "end": v(-76.65, 41.66) * mm});
            skLineSegment(sketch, "E1023", {"start": v(-76.65, 41.66) * mm, "end": v(-73.4, 42.08) * mm});
            skLineSegment(sketch, "E1024", {"start": v(-73.4, 42.08) * mm, "end": v(-72.33, 42.08) * mm});
            skLineSegment(sketch, "E1025", {"start": v(-72.33, 42.08) * mm, "end": v(-71.25, 42.08) * mm});
            skLineSegment(sketch, "E1026", {"start": v(-71.25, 42.08) * mm, "end": v(-68, 41.66) * mm});
            skLineSegment(sketch, "E1027", {"start": v(-68, 41.66) * mm, "end": v(-63.98, 40.45) * mm});
            skLineSegment(sketch, "E1028", {"start": v(-63.98, 40.45) * mm, "end": v(-60.34, 38.53) * mm});
            skLineSegment(sketch, "E1029", {"start": v(-60.34, 38.53) * mm, "end": v(-57.17, 36) * mm});
            skLineSegment(sketch, "E1030", {"start": v(-57.17, 36) * mm, "end": v(-54.56, 32.92) * mm});
            skLineSegment(sketch, "E1031", {"start": v(-54.56, 32.92) * mm, "end": v(-52.58, 29.39) * mm});
            skLineSegment(sketch, "E1032", {"start": v(-52.58, 29.39) * mm, "end": v(-51.33, 25.5) * mm});
            skLineSegment(sketch, "E1033", {"start": v(-51.33, 25.5) * mm, "end": v(-50.9, 22.35) * mm});
            skLineSegment(sketch, "E1034", {"start": v(-50.9, 22.35) * mm, "end": v(-50.9, 21.3) * mm});
            skLineSegment(sketch, "E1035", {"start": v(-50.9, 21.3) * mm, "end": v(-50.9, 20.26) * mm});
            skLineSegment(sketch, "E1036", {"start": v(-50.9, 20.26) * mm, "end": v(-51.33, 17.12) * mm});
            skLineSegment(sketch, "E1037", {"start": v(-51.33, 17.12) * mm, "end": v(-52.58, 13.22) * mm});
            skLineSegment(sketch, "E1038", {"start": v(-52.58, 13.22) * mm, "end": v(-54.56, 9.69) * mm});
            skLineSegment(sketch, "E1039", {"start": v(-54.56, 9.69) * mm, "end": v(-57.17, 6.61) * mm});
            skLineSegment(sketch, "E1040", {"start": v(-57.17, 6.61) * mm, "end": v(-60.34, 4.07) * mm});
            skLineSegment(sketch, "E1041", {"start": v(-60.34, 4.07) * mm, "end": v(-63.98, 2.16) * mm});
            skLineSegment(sketch, "E1042", {"start": v(-63.98, 2.16) * mm, "end": v(-68, 0.95) * mm});
            skLineSegment(sketch, "E1043", {"start": v(-68, 0.95) * mm, "end": v(-71.25, 0.52) * mm});
            skLineSegment(sketch, "E1044", {"start": v(-71.25, 0.52) * mm, "end": v(-72.33, 0.52) * mm});
            skLineSegment(sketch, "E1045.bottom", {"start": v(-114.91, 64.04) * mm, "end": v(125.09, 64.04) * mm});
            skLineSegment(sketch, "E1045.top", {"start": v(-114.91, -28.1) * mm, "end": v(125.09, -28.1) * mm});
            skLineSegment(sketch, "E1045.left", {"start": v(-114.91, 64.04) * mm, "end": v(-114.91, -28.1) * mm});
            skLineSegment(sketch, "E1045.right", {"start": v(125.09, 64.04) * mm, "end": v(125.09, -28.1) * mm});
            skSolve(sketch);
        }
        {
            var Q0;
            Q0 = qSketchRegion(id + "F0", true);
            var Q1;
            Q1=makeQuery(id+"F0.imprint","IMPRINT",FACE,{"disambiguationData":[TD([[makeQuery(id+"F0.imprint","IMPRINT",EDGE,{"derivedFrom":sQuery(id+"F0.wireOp",EDGE,"E697")}),1.0]])]});
            var Q2;
            Q2=makeQuery(id+"F0.imprint","IMPRINT",FACE,{"disambiguationData":[TD([[makeQuery(id+"F0.imprint","IMPRINT",EDGE,{"derivedFrom":sQuery(id+"F0.wireOp",EDGE,"E841")}),1.0]])]});
            var Q3;
            Q3=makeQuery(id+"F0.imprint","IMPRINT",FACE,{"disambiguationData":[TD([[makeQuery(id+"F0.imprint","IMPRINT",EDGE,{"derivedFrom":sQuery(id+"F0.wireOp",EDGE,"E1")}),-1.0]])]});
            var Q4;
            Q4=makeQuery(id+"F0.imprint","IMPRINT",FACE,{"disambiguationData":[TD([[makeQuery(id+"F0.imprint","IMPRINT",EDGE,{"derivedFrom":sQuery(id+"F0.wireOp",EDGE,"E84")}),-1.0]])]});
            var Q5;
            Q5=makeQuery(id+"F0.imprint","IMPRINT",FACE,{"disambiguationData":[TD([[makeQuery(id+"F0.imprint","IMPRINT",EDGE,{"derivedFrom":sQuery(id+"F0.wireOp",EDGE,"E274")}),-1.0]])]});
            var Q6;
            Q6=makeQuery(id+"F0.imprint","IMPRINT",FACE,{"disambiguationData":[TD([[makeQuery(id+"F0.imprint","IMPRINT",EDGE,{"derivedFrom":sQuery(id+"F0.wireOp",EDGE,"E416")}),1.0]])]});
            var Q7;
            Q7=makeQuery(id+"F0.imprint","IMPRINT",FACE,{"disambiguationData":[TD([[makeQuery(id+"F0.imprint","IMPRINT",EDGE,{"derivedFrom":sQuery(id+"F0.wireOp",EDGE,"E530")}),1.0]])]});
            var Q8;
            Q8=makeQuery(id+"F0.imprint","IMPRINT",FACE,{"disambiguationData":[TD([[makeQuery(id+"F0.imprint","IMPRINT",EDGE,{"derivedFrom":sQuery(id+"F0.wireOp",EDGE,"E932")}),1.0]])]});
            var Q9;
            Q9=makeQuery(id+"F0.imprint","IMPRINT",FACE,{"disambiguationData":[TD([[makeQuery(id+"F0.imprint","IMPRINT",EDGE,{"derivedFrom":sQuery(id+"F0.wireOp",EDGE,"E339")}),-1.0]])]});
            var Q10;
            Q10=makeQuery(id+"F0.imprint","IMPRINT",FACE,{"disambiguationData":[TD([[makeQuery(id+"F0.imprint","IMPRINT",EDGE,{"derivedFrom":sQuery(id+"F0.wireOp",EDGE,"E448")}),-1.0]])]});
            var Q11;
            Q11=makeQuery(id+"F0.imprint","IMPRINT",FACE,{"disambiguationData":[TD([[makeQuery(id+"F0.imprint","IMPRINT",EDGE,{"derivedFrom":sQuery(id+"F0.wireOp",EDGE,"E1")}),1.0]])]});
            var Q12;
            Q12=makeQuery(id+"F0.imprint","IMPRINT",FACE,{"disambiguationData":[TD([[makeQuery(id+"F0.imprint","IMPRINT",EDGE,{"derivedFrom":sQuery(id+"F0.wireOp",EDGE,"E697")}),-1.0]])]});
            var Q13;
            Q13=makeQuery(id+"F0.imprint","IMPRINT",FACE,{"disambiguationData":[TD([[makeQuery(id+"F0.imprint","IMPRINT",EDGE,{"derivedFrom":sQuery(id+"F0.wireOp",EDGE,"E965")}),1.0]])]});
            var Q14;
            Q14=makeQuery(id+"F0.imprint","IMPRINT",FACE,{"disambiguationData":[TD([[makeQuery(id+"F0.imprint","IMPRINT",EDGE,{"derivedFrom":sQuery(id+"F0.wireOp",EDGE,"E118")}),-1.0]])]});
            var Q15;
            Q15=makeQuery(id+"F0.imprint","IMPRINT",FACE,{"disambiguationData":[TD([[makeQuery(id+"F0.imprint","IMPRINT",EDGE,{"derivedFrom":sQuery(id+"F0.wireOp",EDGE,"E541")}),-1.0]])]});
            var Q16;
            Q16=makeQuery(id+"F0.imprint","IMPRINT",FACE,{"disambiguationData":[TD([[makeQuery(id+"F0.imprint","IMPRINT",EDGE,{"derivedFrom":sQuery(id+"F0.wireOp",EDGE,"04ef46ec-d390-4558-bebd-80a1764d6b11")}),-1.0]])]});
            var Q17;
            {var subQ0=sQuery(id+"F0.wireOp",EDGE,"904b6fe3-4e82-4cbc-b9d6-a78c2d503d77");Q17=makeQuery(id+"F0.imprint","IMPRINT",FACE,{"disambiguationData":[TD([[makeQuery(id+"F0.imprint","IMPRINT",EDGE,{"derivedFrom":subQ0}),1.0]])]});}
            var Q18;
            Q18=makeQuery(id+"F0.imprint","IMPRINT",FACE,{"disambiguationData":[TD([[makeQuery(id+"F0.imprint","IMPRINT",EDGE,{"derivedFrom":sQuery(id+"F0.wireOp",EDGE,"ced4354c-1389-40cb-9ddd-71df8297f284")}),-1.0]])]});
            extrude(context, id + "F1", {"entities" : qUnion([Q0, Q1, Q2, Q3, Q4, Q5, Q6, Q7, Q8, Q9, Q10, Q11, Q12, Q13, Q14, Q15, Q16, Q17, Q18]), "oppositeDirection" : true, "depth" : 1 * mm, "offsetDistance" : 25 * mm});
        }
        {
            var Q0;
            Q0=makeQuery(id+"F0.imprint","IMPRINT",FACE,{"disambiguationData":[TD([[makeQuery(id+"F0.imprint","IMPRINT",EDGE,{"derivedFrom":sQuery(id+"F0.wireOp",EDGE,"E1")}),-1.0]])]});
            var Q1;
            Q1=makeQuery(id+"F0.imprint","IMPRINT",FACE,{"disambiguationData":[TD([[makeQuery(id+"F0.imprint","IMPRINT",EDGE,{"derivedFrom":sQuery(id+"F0.wireOp",EDGE,"E965")}),1.0]])]});
            var Q2;
            Q2=makeQuery(id+"F0.imprint","IMPRINT",FACE,{"disambiguationData":[TD([[makeQuery(id+"F0.imprint","IMPRINT",EDGE,{"derivedFrom":sQuery(id+"F0.wireOp",EDGE,"E84")}),-1.0]])]});
            var Q3;
            Q3=makeQuery(id+"F0.imprint","IMPRINT",FACE,{"disambiguationData":[TD([[makeQuery(id+"F0.imprint","IMPRINT",EDGE,{"derivedFrom":sQuery(id+"F0.wireOp",EDGE,"E118")}),-1.0]])]});
            var Q4;
            Q4=makeQuery(id+"F0.imprint","IMPRINT",FACE,{"disambiguationData":[TD([[makeQuery(id+"F0.imprint","IMPRINT",EDGE,{"derivedFrom":sQuery(id+"F0.wireOp",EDGE,"E274")}),-1.0]])]});
            var Q5;
            Q5=makeQuery(id+"F0.imprint","IMPRINT",FACE,{"disambiguationData":[TD([[makeQuery(id+"F0.imprint","IMPRINT",EDGE,{"derivedFrom":sQuery(id+"F0.wireOp",EDGE,"E339")}),-1.0]])]});
            var Q6;
            Q6=makeQuery(id+"F0.imprint","IMPRINT",FACE,{"disambiguationData":[TD([[makeQuery(id+"F0.imprint","IMPRINT",EDGE,{"derivedFrom":sQuery(id+"F0.wireOp",EDGE,"E448")}),-1.0]])]});
            var Q7;
            Q7=makeQuery(id+"F0.imprint","IMPRINT",FACE,{"disambiguationData":[TD([[makeQuery(id+"F0.imprint","IMPRINT",EDGE,{"derivedFrom":sQuery(id+"F0.wireOp",EDGE,"E541")}),-1.0]])]});
            var Q8;
            Q8=makeQuery(id+"F0.imprint","IMPRINT",FACE,{"disambiguationData":[TD([[makeQuery(id+"F0.imprint","IMPRINT",EDGE,{"derivedFrom":sQuery(id+"F0.wireOp",EDGE,"E932")}),1.0]])]});
            var Q9;
            Q9=makeQuery(id+"F0.imprint","IMPRINT",FACE,{"disambiguationData":[TD([[makeQuery(id+"F0.imprint","IMPRINT",EDGE,{"derivedFrom":sQuery(id+"F0.wireOp",EDGE,"E841")}),1.0]])]});
            var Q10;
            Q10=makeQuery(id+"F0.imprint","IMPRINT",FACE,{"disambiguationData":[TD([[makeQuery(id+"F0.imprint","IMPRINT",EDGE,{"derivedFrom":sQuery(id+"F0.wireOp",EDGE,"E697")}),1.0]])]});
            extrude(context, id + "F2", {"entities" : qUnion([Q0, Q1, Q2, Q3, Q4, Q5, Q6, Q7, Q8, Q9, Q10]), "operationType" : NewBodyOperationType.ADD, "depth" : 2 * mm, "offsetDistance" : 25 * mm});
        }
    });
